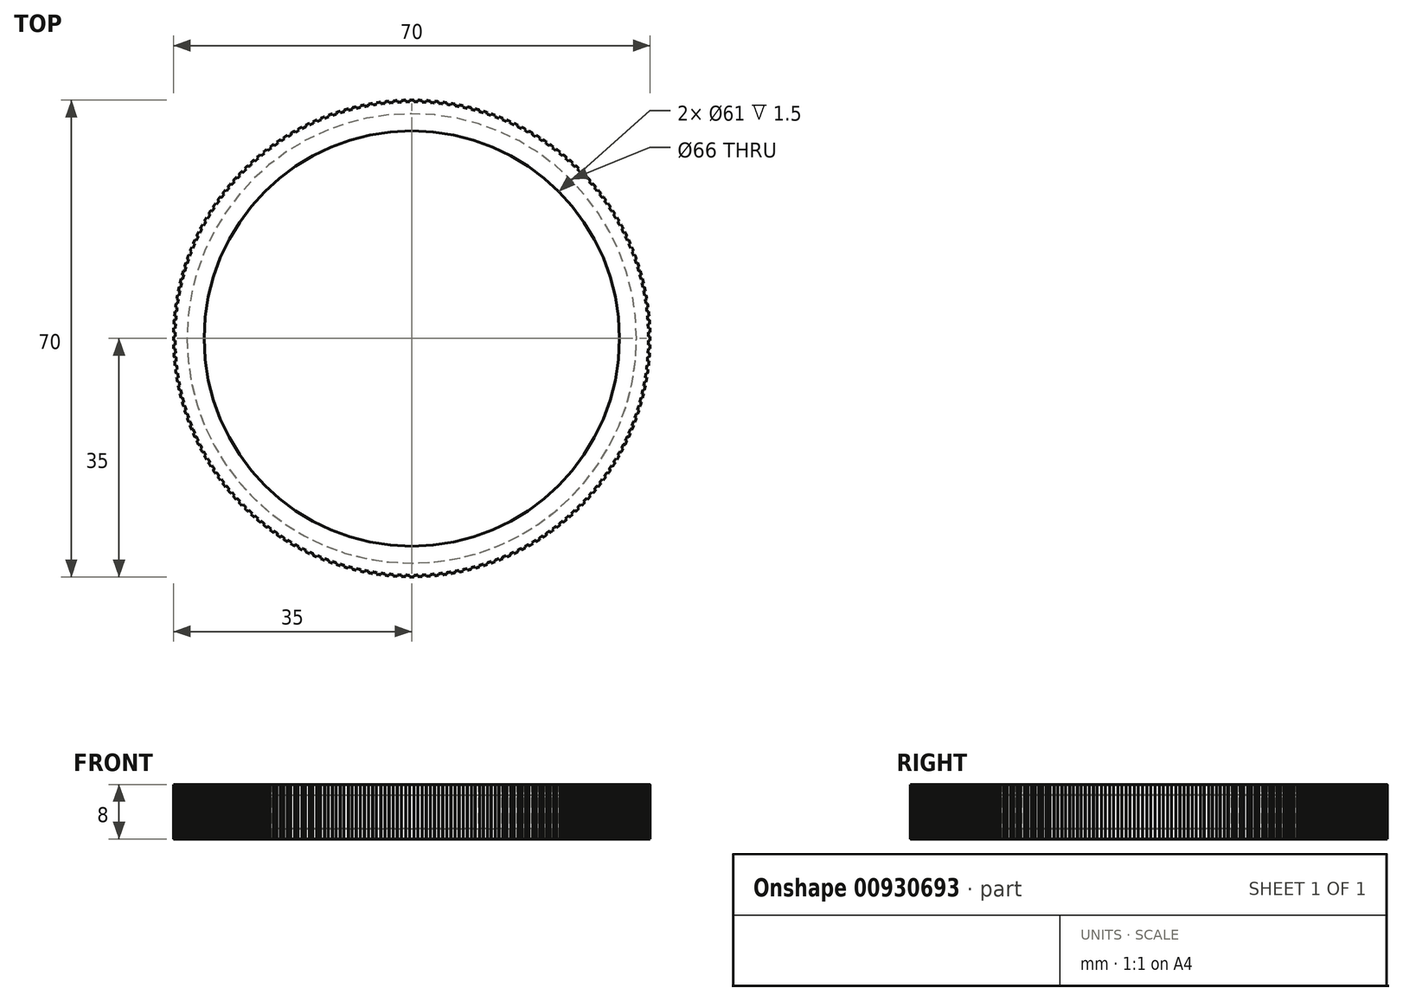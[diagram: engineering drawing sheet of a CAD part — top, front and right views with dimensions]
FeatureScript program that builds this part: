
annotation { "Feature Type Name" : "Feature", "Feature Type Description" : "" }
export const myFeature = defineFeature(function(context is Context, id is Id, definition is map)
    precondition{}
    {
        {
            var Q0;
            Q0=qCreatedBy(makeId("Front.planeOp"),FACE);
            var sketch = newSketch(context, id + "F0", { "sketchPlane" : qUnion([Q0])});
            skLineSegment(sketch, "E0.bottom", {"start": v(30.5, 8) * mm, "end": v(35, 8) * mm});
            skLineSegment(sketch, "E0.top", {"start": v(30.5, 0) * mm, "end": v(35, 0) * mm});
            skLineSegment(sketch, "E0.left", {"start": v(30.5, 8) * mm, "end": v(30.5, 6.5) * mm});
            skLineSegment(sketch, "E0.right", {"start": v(35, 8) * mm, "end": v(35, 0) * mm});
            skLineSegment(sketch, "E1", {"start": v(30.5, 6.5) * mm, "end": v(33, 6.5) * mm});
            skLineSegment(sketch, "E2", {"start": v(33, 6.5) * mm, "end": v(33, 1.5) * mm});
            skLineSegment(sketch, "E3", {"start": v(33, 1.5) * mm, "end": v(30.5, 1.5) * mm});
            skLineSegment(sketch, "E4.trimOffspring", {"start": v(30.5, 1.5) * mm, "end": v(30.5, 0) * mm});
            skLineSegment(sketch, "E5", {"start": v(0, 0) * mm, "end": v(0, 10) * mm, "construction": true});
            skSolve(sketch);
        }
        {
            var Q0;
            Q0=qSketchRegion(id+"F0",true);
            var Q1;
            Q1=sQuery(id+"F0.wireOp",EDGE,"E5");
            revolve(context, id + "F1", {"entities" : qUnion([Q0]), "axis" : qUnion([Q1]), "revolveType" : RevolveType.FULL});
        }
        {
            var Q0;
            Q0=makeQuery(id+"F1.opRevolve","SWEPT_EDGE",EDGE,{"disambiguationData":[OSD([sQuery(id+"F0.wireOp",EDGE,"E1"),sQuery(id+"F0.wireOp",EDGE,"E2")])]});
            var Q1;
            Q1=makeQuery(id+"F1.opRevolve","SWEPT_EDGE",EDGE,{"disambiguationData":[OSD([sQuery(id+"F0.wireOp",EDGE,"E2"),sQuery(id+"F0.wireOp",EDGE,"E3")])]});
            fillet(context, id + "F2", {"entities" : qUnion([Q0, Q1]), "radius" : 1 * mm, "tangentPropagation" : true, "allowEdgeOverflow" : false});
        }
        {
            var Q0;
            Q0=makeQuery(id+"F1.opRevolve","SWEPT_FACE",FACE,{"disambiguationData":[OSD([sQuery(id+"F0.wireOp",EDGE,"E0.bottom")])]});
            var sketch = newSketch(context, id + "F3", { "sketchPlane" : qUnion([Q0])});
            skLineSegment(sketch, "E6", {"start": v(0.3, 35) * mm, "end": v(0, 0) * mm, "construction": true});
            skLineSegment(sketch, "E7", {"start": v(0, 0) * mm, "end": v(0.92, 34.99) * mm, "construction": true});
            skCircle(sketch, "E8", {"center": v(0, 0) * mm, "radius": 34.75 * mm, "construction": true});
            skArc(sketch, "E9", {"start": v(0.92, 34.99) * mm, "mid": v(0.61, 35) * mm, "end": v(0.3, 35) * mm});
            skArc(sketch, "E10", {"start": v(0.9, 34.74) * mm, "mid": v(0.6, 34.74) * mm, "end": v(0.3, 34.75) * mm});
            skLineSegment(sketch, "E11", {"start": v(0.3, 35) * mm, "end": v(0.3, 34.75) * mm});
            skLineSegment(sketch, "E12", {"start": v(0.92, 34.99) * mm, "end": v(0.9, 34.74) * mm});
            skLineSegment(sketch, "E13.1.0", {"start": v(2.14, 34.93) * mm, "end": v(2.12, 34.69) * mm});
            skArc(sketch, "E13.1.1", {"start": v(2.12, 34.69) * mm, "mid": v(1.82, 34.7) * mm, "end": v(1.52, 34.72) * mm});
            skLineSegment(sketch, "E13.1.2", {"start": v(1.53, 34.97) * mm, "end": v(1.52, 34.72) * mm});
            skArc(sketch, "E13.1.3", {"start": v(2.14, 34.93) * mm, "mid": v(1.83, 34.95) * mm, "end": v(1.53, 34.97) * mm});
            skLineSegment(sketch, "E13.2.0", {"start": v(3.35, 34.84) * mm, "end": v(3.33, 34.6) * mm});
            skArc(sketch, "E13.2.1", {"start": v(3.33, 34.6) * mm, "mid": v(3.03, 34.62) * mm, "end": v(2.73, 34.64) * mm});
            skLineSegment(sketch, "E13.2.2", {"start": v(2.75, 34.9) * mm, "end": v(2.73, 34.64) * mm});
            skArc(sketch, "E13.2.3", {"start": v(3.35, 34.84) * mm, "mid": v(3.05, 34.87) * mm, "end": v(2.75, 34.9) * mm});
            skLineSegment(sketch, "E13.3.0", {"start": v(4.57, 34.7) * mm, "end": v(4.54, 34.45) * mm});
            skArc(sketch, "E13.3.1", {"start": v(4.54, 34.45) * mm, "mid": v(4.23, 34.5) * mm, "end": v(3.93, 34.53) * mm});
            skLineSegment(sketch, "E13.3.2", {"start": v(3.96, 34.78) * mm, "end": v(3.93, 34.53) * mm});
            skArc(sketch, "E13.3.3", {"start": v(4.57, 34.7) * mm, "mid": v(4.27, 34.74) * mm, "end": v(3.96, 34.78) * mm});
            skLineSegment(sketch, "E13.4.0", {"start": v(5.78, 34.52) * mm, "end": v(5.74, 34.27) * mm});
            skArc(sketch, "E13.4.1", {"start": v(5.74, 34.27) * mm, "mid": v(5.44, 34.32) * mm, "end": v(5.14, 34.37) * mm});
            skLineSegment(sketch, "E13.4.2", {"start": v(5.17, 34.62) * mm, "end": v(5.14, 34.37) * mm});
            skArc(sketch, "E13.4.3", {"start": v(5.78, 34.52) * mm, "mid": v(5.48, 34.57) * mm, "end": v(5.17, 34.62) * mm});
            skLineSegment(sketch, "E13.5.0", {"start": v(6.98, 34.3) * mm, "end": v(6.93, 34.05) * mm});
            skArc(sketch, "E13.5.1", {"start": v(6.93, 34.05) * mm, "mid": v(6.63, 34.11) * mm, "end": v(6.33, 34.17) * mm});
            skLineSegment(sketch, "E13.5.2", {"start": v(6.38, 34.41) * mm, "end": v(6.33, 34.17) * mm});
            skArc(sketch, "E13.5.3", {"start": v(6.98, 34.3) * mm, "mid": v(6.68, 34.36) * mm, "end": v(6.38, 34.41) * mm});
            skLineSegment(sketch, "E13.6.0", {"start": v(8.17, 34.03) * mm, "end": v(8.11, 33.79) * mm});
            skArc(sketch, "E13.6.1", {"start": v(8.11, 33.79) * mm, "mid": v(7.82, 33.86) * mm, "end": v(7.52, 33.93) * mm});
            skLineSegment(sketch, "E13.6.2", {"start": v(7.58, 34.17) * mm, "end": v(7.52, 33.93) * mm});
            skArc(sketch, "E13.6.3", {"start": v(8.17, 34.03) * mm, "mid": v(7.87, 34.1) * mm, "end": v(7.58, 34.17) * mm});
            skLineSegment(sketch, "E13.7.0", {"start": v(9.35, 33.73) * mm, "end": v(9.29, 33.49) * mm});
            skArc(sketch, "E13.7.1", {"start": v(9.29, 33.49) * mm, "mid": v(9, 33.57) * mm, "end": v(8.7, 33.64) * mm});
            skLineSegment(sketch, "E13.7.2", {"start": v(8.76, 33.89) * mm, "end": v(8.7, 33.64) * mm});
            skArc(sketch, "E13.7.3", {"start": v(9.35, 33.73) * mm, "mid": v(9.06, 33.8) * mm, "end": v(8.76, 33.89) * mm});
            skLineSegment(sketch, "E13.8.0", {"start": v(10.52, 33.38) * mm, "end": v(10.45, 33.14) * mm});
            skArc(sketch, "E13.8.1", {"start": v(10.45, 33.14) * mm, "mid": v(10.16, 33.23) * mm, "end": v(9.87, 33.32) * mm});
            skLineSegment(sketch, "E13.8.2", {"start": v(9.94, 33.56) * mm, "end": v(9.87, 33.32) * mm});
            skArc(sketch, "E13.8.3", {"start": v(10.52, 33.38) * mm, "mid": v(10.23, 33.47) * mm, "end": v(9.94, 33.56) * mm});
            skLineSegment(sketch, "E13.9.0", {"start": v(11.68, 33) * mm, "end": v(11.6, 32.76) * mm});
            skArc(sketch, "E13.9.1", {"start": v(11.6, 32.76) * mm, "mid": v(11.31, 32.86) * mm, "end": v(11.03, 32.95) * mm});
            skLineSegment(sketch, "E13.9.2", {"start": v(11.1, 33.2) * mm, "end": v(11.03, 32.95) * mm});
            skArc(sketch, "E13.9.3", {"start": v(11.68, 33) * mm, "mid": v(11.4, 33.1) * mm, "end": v(11.1, 33.2) * mm});
            skLineSegment(sketch, "E13.10.0", {"start": v(12.83, 32.56) * mm, "end": v(12.74, 32.33) * mm});
            skArc(sketch, "E13.10.1", {"start": v(12.74, 32.33) * mm, "mid": v(12.45, 32.44) * mm, "end": v(12.17, 32.55) * mm});
            skLineSegment(sketch, "E13.10.2", {"start": v(12.26, 32.78) * mm, "end": v(12.17, 32.55) * mm});
            skArc(sketch, "E13.10.3", {"start": v(12.83, 32.56) * mm, "mid": v(12.54, 32.68) * mm, "end": v(12.26, 32.78) * mm});
            skLineSegment(sketch, "E13.11.0", {"start": v(13.96, 32.1) * mm, "end": v(13.86, 31.87) * mm});
            skArc(sketch, "E13.11.1", {"start": v(13.86, 31.87) * mm, "mid": v(13.58, 31.99) * mm, "end": v(13.3, 32.1) * mm});
            skLineSegment(sketch, "E13.11.2", {"start": v(13.4, 32.34) * mm, "end": v(13.3, 32.1) * mm});
            skArc(sketch, "E13.11.3", {"start": v(13.96, 32.1) * mm, "mid": v(13.68, 32.22) * mm, "end": v(13.4, 32.34) * mm});
            skLineSegment(sketch, "E13.12.0", {"start": v(15.07, 31.6) * mm, "end": v(14.96, 31.36) * mm});
            skArc(sketch, "E13.12.1", {"start": v(14.96, 31.36) * mm, "mid": v(14.69, 31.5) * mm, "end": v(14.41, 31.62) * mm});
            skLineSegment(sketch, "E13.12.2", {"start": v(14.51, 31.85) * mm, "end": v(14.41, 31.62) * mm});
            skArc(sketch, "E13.12.3", {"start": v(15.07, 31.6) * mm, "mid": v(14.8, 31.72) * mm, "end": v(14.51, 31.85) * mm});
            skLineSegment(sketch, "E13.13.0", {"start": v(16.16, 31.05) * mm, "end": v(16.05, 30.82) * mm});
            skArc(sketch, "E13.13.1", {"start": v(16.05, 30.82) * mm, "mid": v(15.78, 30.96) * mm, "end": v(15.5, 31.1) * mm});
            skLineSegment(sketch, "E13.13.2", {"start": v(15.62, 31.32) * mm, "end": v(15.5, 31.1) * mm});
            skArc(sketch, "E13.13.3", {"start": v(16.16, 31.05) * mm, "mid": v(15.89, 31.19) * mm, "end": v(15.62, 31.32) * mm});
            skLineSegment(sketch, "E13.14.0", {"start": v(17.23, 30.46) * mm, "end": v(17.11, 30.24) * mm});
            skArc(sketch, "E13.14.1", {"start": v(17.11, 30.24) * mm, "mid": v(16.85, 30.4) * mm, "end": v(16.58, 30.54) * mm});
            skLineSegment(sketch, "E13.14.2", {"start": v(16.7, 30.76) * mm, "end": v(16.58, 30.54) * mm});
            skArc(sketch, "E13.14.3", {"start": v(17.23, 30.46) * mm, "mid": v(16.97, 30.61) * mm, "end": v(16.7, 30.76) * mm});
            skLineSegment(sketch, "E13.15.0", {"start": v(18.29, 29.84) * mm, "end": v(18.16, 29.63) * mm});
            skArc(sketch, "E13.15.1", {"start": v(18.16, 29.63) * mm, "mid": v(17.9, 29.79) * mm, "end": v(17.64, 29.94) * mm});
            skLineSegment(sketch, "E13.15.2", {"start": v(17.76, 30.16) * mm, "end": v(17.64, 29.94) * mm});
            skArc(sketch, "E13.15.3", {"start": v(18.29, 29.84) * mm, "mid": v(18.03, 30) * mm, "end": v(17.76, 30.16) * mm});
            skLineSegment(sketch, "E13.16.0", {"start": v(19.32, 29.19) * mm, "end": v(19.18, 28.98) * mm});
            skArc(sketch, "E13.16.1", {"start": v(19.18, 28.98) * mm, "mid": v(18.93, 29.14) * mm, "end": v(18.67, 29.3) * mm});
            skLineSegment(sketch, "E13.16.2", {"start": v(18.8, 29.52) * mm, "end": v(18.67, 29.3) * mm});
            skArc(sketch, "E13.16.3", {"start": v(19.32, 29.19) * mm, "mid": v(19.06, 29.35) * mm, "end": v(18.8, 29.52) * mm});
            skLineSegment(sketch, "E13.17.0", {"start": v(20.32, 28.5) * mm, "end": v(20.18, 28.3) * mm});
            skArc(sketch, "E13.17.1", {"start": v(20.18, 28.3) * mm, "mid": v(19.93, 28.47) * mm, "end": v(19.68, 28.64) * mm});
            skLineSegment(sketch, "E13.17.2", {"start": v(19.82, 28.84) * mm, "end": v(19.68, 28.64) * mm});
            skArc(sketch, "E13.17.3", {"start": v(20.32, 28.5) * mm, "mid": v(20.08, 28.67) * mm, "end": v(19.82, 28.84) * mm});
            skLineSegment(sketch, "E13.18.0", {"start": v(21.3, 27.77) * mm, "end": v(21.15, 27.57) * mm});
            skArc(sketch, "E13.18.1", {"start": v(21.15, 27.57) * mm, "mid": v(20.91, 27.75) * mm, "end": v(20.67, 27.93) * mm});
            skLineSegment(sketch, "E13.18.2", {"start": v(20.82, 28.13) * mm, "end": v(20.67, 27.93) * mm});
            skArc(sketch, "E13.18.3", {"start": v(21.3, 27.77) * mm, "mid": v(21.06, 27.95) * mm, "end": v(20.82, 28.13) * mm});
            skLineSegment(sketch, "E13.19.0", {"start": v(22.26, 27) * mm, "end": v(22.1, 26.81) * mm});
            skArc(sketch, "E13.19.1", {"start": v(22.1, 26.81) * mm, "mid": v(21.87, 27) * mm, "end": v(21.63, 27.2) * mm});
            skLineSegment(sketch, "E13.19.2", {"start": v(21.79, 27.4) * mm, "end": v(21.63, 27.2) * mm});
            skArc(sketch, "E13.19.3", {"start": v(22.26, 27) * mm, "mid": v(22.03, 27.2) * mm, "end": v(21.79, 27.4) * mm});
            skLineSegment(sketch, "E13.20.0", {"start": v(23.2, 26.21) * mm, "end": v(23.03, 26.03) * mm});
            skArc(sketch, "E13.20.1", {"start": v(23.03, 26.03) * mm, "mid": v(22.8, 26.23) * mm, "end": v(22.57, 26.42) * mm});
            skLineSegment(sketch, "E13.20.2", {"start": v(22.73, 26.61) * mm, "end": v(22.57, 26.42) * mm});
            skArc(sketch, "E13.20.3", {"start": v(23.2, 26.21) * mm, "mid": v(22.96, 26.41) * mm, "end": v(22.73, 26.61) * mm});
            skLineSegment(sketch, "E13.21.0", {"start": v(24.1, 25.39) * mm, "end": v(23.92, 25.2) * mm});
            skArc(sketch, "E13.21.1", {"start": v(23.92, 25.2) * mm, "mid": v(23.7, 25.41) * mm, "end": v(23.48, 25.62) * mm});
            skLineSegment(sketch, "E13.21.2", {"start": v(23.65, 25.8) * mm, "end": v(23.48, 25.62) * mm});
            skArc(sketch, "E13.21.3", {"start": v(24.1, 25.39) * mm, "mid": v(23.87, 25.6) * mm, "end": v(23.65, 25.8) * mm});
            skLineSegment(sketch, "E13.22.0", {"start": v(24.96, 24.53) * mm, "end": v(24.79, 24.36) * mm});
            skArc(sketch, "E13.22.1", {"start": v(24.79, 24.36) * mm, "mid": v(24.57, 24.57) * mm, "end": v(24.36, 24.79) * mm});
            skLineSegment(sketch, "E13.22.2", {"start": v(24.53, 24.96) * mm, "end": v(24.36, 24.79) * mm});
            skArc(sketch, "E13.22.3", {"start": v(24.96, 24.53) * mm, "mid": v(24.75, 24.75) * mm, "end": v(24.53, 24.96) * mm});
            skLineSegment(sketch, "E13.23.0", {"start": v(25.8, 23.65) * mm, "end": v(25.62, 23.48) * mm});
            skArc(sketch, "E13.23.1", {"start": v(25.62, 23.48) * mm, "mid": v(25.41, 23.7) * mm, "end": v(25.2, 23.92) * mm});
            skLineSegment(sketch, "E13.23.2", {"start": v(25.39, 24.1) * mm, "end": v(25.2, 23.92) * mm});
            skArc(sketch, "E13.23.3", {"start": v(25.8, 23.65) * mm, "mid": v(25.6, 23.87) * mm, "end": v(25.39, 24.1) * mm});
            skLineSegment(sketch, "E13.24.0", {"start": v(26.61, 22.73) * mm, "end": v(26.42, 22.57) * mm});
            skArc(sketch, "E13.24.1", {"start": v(26.42, 22.57) * mm, "mid": v(26.23, 22.8) * mm, "end": v(26.03, 23.03) * mm});
            skLineSegment(sketch, "E13.24.2", {"start": v(26.21, 23.2) * mm, "end": v(26.03, 23.03) * mm});
            skArc(sketch, "E13.24.3", {"start": v(26.61, 22.73) * mm, "mid": v(26.41, 22.96) * mm, "end": v(26.21, 23.2) * mm});
            skLineSegment(sketch, "E13.25.0", {"start": v(27.4, 21.79) * mm, "end": v(27.2, 21.63) * mm});
            skArc(sketch, "E13.25.1", {"start": v(27.2, 21.63) * mm, "mid": v(27, 21.87) * mm, "end": v(26.81, 22.1) * mm});
            skLineSegment(sketch, "E13.25.2", {"start": v(27, 22.26) * mm, "end": v(26.81, 22.1) * mm});
            skArc(sketch, "E13.25.3", {"start": v(27.4, 21.79) * mm, "mid": v(27.2, 22.03) * mm, "end": v(27, 22.26) * mm});
            skLineSegment(sketch, "E13.26.0", {"start": v(28.13, 20.82) * mm, "end": v(27.93, 20.67) * mm});
            skArc(sketch, "E13.26.1", {"start": v(27.93, 20.67) * mm, "mid": v(27.75, 20.91) * mm, "end": v(27.57, 21.15) * mm});
            skLineSegment(sketch, "E13.26.2", {"start": v(27.77, 21.3) * mm, "end": v(27.57, 21.15) * mm});
            skArc(sketch, "E13.26.3", {"start": v(28.13, 20.82) * mm, "mid": v(27.95, 21.06) * mm, "end": v(27.77, 21.3) * mm});
            skLineSegment(sketch, "E13.27.0", {"start": v(28.84, 19.82) * mm, "end": v(28.64, 19.68) * mm});
            skArc(sketch, "E13.27.1", {"start": v(28.64, 19.68) * mm, "mid": v(28.47, 19.93) * mm, "end": v(28.3, 20.18) * mm});
            skLineSegment(sketch, "E13.27.2", {"start": v(28.5, 20.32) * mm, "end": v(28.3, 20.18) * mm});
            skArc(sketch, "E13.27.3", {"start": v(28.84, 19.82) * mm, "mid": v(28.67, 20.08) * mm, "end": v(28.5, 20.32) * mm});
            skLineSegment(sketch, "E13.28.0", {"start": v(29.52, 18.8) * mm, "end": v(29.3, 18.67) * mm});
            skArc(sketch, "E13.28.1", {"start": v(29.3, 18.67) * mm, "mid": v(29.14, 18.93) * mm, "end": v(28.98, 19.18) * mm});
            skLineSegment(sketch, "E13.28.2", {"start": v(29.19, 19.32) * mm, "end": v(28.98, 19.18) * mm});
            skArc(sketch, "E13.28.3", {"start": v(29.52, 18.8) * mm, "mid": v(29.35, 19.06) * mm, "end": v(29.19, 19.32) * mm});
            skLineSegment(sketch, "E13.29.0", {"start": v(30.16, 17.76) * mm, "end": v(29.94, 17.64) * mm});
            skArc(sketch, "E13.29.1", {"start": v(29.94, 17.64) * mm, "mid": v(29.79, 17.9) * mm, "end": v(29.63, 18.16) * mm});
            skLineSegment(sketch, "E13.29.2", {"start": v(29.84, 18.29) * mm, "end": v(29.63, 18.16) * mm});
            skArc(sketch, "E13.29.3", {"start": v(30.16, 17.76) * mm, "mid": v(30, 18.03) * mm, "end": v(29.84, 18.29) * mm});
            skLineSegment(sketch, "E13.30.0", {"start": v(30.76, 16.7) * mm, "end": v(30.54, 16.58) * mm});
            skArc(sketch, "E13.30.1", {"start": v(30.54, 16.58) * mm, "mid": v(30.4, 16.85) * mm, "end": v(30.24, 17.11) * mm});
            skLineSegment(sketch, "E13.30.2", {"start": v(30.46, 17.23) * mm, "end": v(30.24, 17.11) * mm});
            skArc(sketch, "E13.30.3", {"start": v(30.76, 16.7) * mm, "mid": v(30.61, 16.97) * mm, "end": v(30.46, 17.23) * mm});
            skLineSegment(sketch, "E13.31.0", {"start": v(31.32, 15.62) * mm, "end": v(31.1, 15.5) * mm});
            skArc(sketch, "E13.31.1", {"start": v(31.1, 15.5) * mm, "mid": v(30.96, 15.78) * mm, "end": v(30.82, 16.05) * mm});
            skLineSegment(sketch, "E13.31.2", {"start": v(31.05, 16.16) * mm, "end": v(30.82, 16.05) * mm});
            skArc(sketch, "E13.31.3", {"start": v(31.32, 15.62) * mm, "mid": v(31.19, 15.89) * mm, "end": v(31.05, 16.16) * mm});
            skLineSegment(sketch, "E13.32.0", {"start": v(31.85, 14.51) * mm, "end": v(31.62, 14.41) * mm});
            skArc(sketch, "E13.32.1", {"start": v(31.62, 14.41) * mm, "mid": v(31.5, 14.69) * mm, "end": v(31.36, 14.96) * mm});
            skLineSegment(sketch, "E13.32.2", {"start": v(31.6, 15.07) * mm, "end": v(31.36, 14.96) * mm});
            skArc(sketch, "E13.32.3", {"start": v(31.85, 14.51) * mm, "mid": v(31.72, 14.8) * mm, "end": v(31.6, 15.07) * mm});
            skLineSegment(sketch, "E13.33.0", {"start": v(32.34, 13.4) * mm, "end": v(32.1, 13.3) * mm});
            skArc(sketch, "E13.33.1", {"start": v(32.1, 13.3) * mm, "mid": v(31.99, 13.58) * mm, "end": v(31.87, 13.86) * mm});
            skLineSegment(sketch, "E13.33.2", {"start": v(32.1, 13.96) * mm, "end": v(31.87, 13.86) * mm});
            skArc(sketch, "E13.33.3", {"start": v(32.34, 13.4) * mm, "mid": v(32.22, 13.68) * mm, "end": v(32.1, 13.96) * mm});
            skLineSegment(sketch, "E13.34.0", {"start": v(32.78, 12.26) * mm, "end": v(32.55, 12.17) * mm});
            skArc(sketch, "E13.34.1", {"start": v(32.55, 12.17) * mm, "mid": v(32.44, 12.45) * mm, "end": v(32.33, 12.74) * mm});
            skLineSegment(sketch, "E13.34.2", {"start": v(32.56, 12.83) * mm, "end": v(32.33, 12.74) * mm});
            skArc(sketch, "E13.34.3", {"start": v(32.78, 12.26) * mm, "mid": v(32.68, 12.54) * mm, "end": v(32.56, 12.83) * mm});
            skLineSegment(sketch, "E13.35.0", {"start": v(33.2, 11.1) * mm, "end": v(32.95, 11.03) * mm});
            skArc(sketch, "E13.35.1", {"start": v(32.95, 11.03) * mm, "mid": v(32.86, 11.31) * mm, "end": v(32.76, 11.6) * mm});
            skLineSegment(sketch, "E13.35.2", {"start": v(33, 11.68) * mm, "end": v(32.76, 11.6) * mm});
            skArc(sketch, "E13.35.3", {"start": v(33.2, 11.1) * mm, "mid": v(33.1, 11.4) * mm, "end": v(33, 11.68) * mm});
            skLineSegment(sketch, "E13.36.0", {"start": v(33.56, 9.94) * mm, "end": v(33.32, 9.87) * mm});
            skArc(sketch, "E13.36.1", {"start": v(33.32, 9.87) * mm, "mid": v(33.23, 10.16) * mm, "end": v(33.14, 10.45) * mm});
            skLineSegment(sketch, "E13.36.2", {"start": v(33.38, 10.52) * mm, "end": v(33.14, 10.45) * mm});
            skArc(sketch, "E13.36.3", {"start": v(33.56, 9.94) * mm, "mid": v(33.47, 10.23) * mm, "end": v(33.38, 10.52) * mm});
            skLineSegment(sketch, "E13.37.0", {"start": v(33.89, 8.76) * mm, "end": v(33.64, 8.7) * mm});
            skArc(sketch, "E13.37.1", {"start": v(33.64, 8.7) * mm, "mid": v(33.57, 9) * mm, "end": v(33.49, 9.29) * mm});
            skLineSegment(sketch, "E13.37.2", {"start": v(33.73, 9.35) * mm, "end": v(33.49, 9.29) * mm});
            skArc(sketch, "E13.37.3", {"start": v(33.89, 8.76) * mm, "mid": v(33.8, 9.06) * mm, "end": v(33.73, 9.35) * mm});
            skLineSegment(sketch, "E13.38.0", {"start": v(34.17, 7.58) * mm, "end": v(33.93, 7.52) * mm});
            skArc(sketch, "E13.38.1", {"start": v(33.93, 7.52) * mm, "mid": v(33.86, 7.82) * mm, "end": v(33.79, 8.11) * mm});
            skLineSegment(sketch, "E13.38.2", {"start": v(34.03, 8.17) * mm, "end": v(33.79, 8.11) * mm});
            skArc(sketch, "E13.38.3", {"start": v(34.17, 7.58) * mm, "mid": v(34.1, 7.87) * mm, "end": v(34.03, 8.17) * mm});
            skLineSegment(sketch, "E13.39.0", {"start": v(34.41, 6.38) * mm, "end": v(34.17, 6.33) * mm});
            skArc(sketch, "E13.39.1", {"start": v(34.17, 6.33) * mm, "mid": v(34.11, 6.63) * mm, "end": v(34.05, 6.93) * mm});
            skLineSegment(sketch, "E13.39.2", {"start": v(34.3, 6.98) * mm, "end": v(34.05, 6.93) * mm});
            skArc(sketch, "E13.39.3", {"start": v(34.41, 6.38) * mm, "mid": v(34.36, 6.68) * mm, "end": v(34.3, 6.98) * mm});
            skLineSegment(sketch, "E13.40.0", {"start": v(34.62, 5.17) * mm, "end": v(34.37, 5.14) * mm});
            skArc(sketch, "E13.40.1", {"start": v(34.37, 5.14) * mm, "mid": v(34.32, 5.44) * mm, "end": v(34.27, 5.74) * mm});
            skLineSegment(sketch, "E13.40.2", {"start": v(34.52, 5.78) * mm, "end": v(34.27, 5.74) * mm});
            skArc(sketch, "E13.40.3", {"start": v(34.62, 5.17) * mm, "mid": v(34.57, 5.48) * mm, "end": v(34.52, 5.78) * mm});
            skLineSegment(sketch, "E13.41.0", {"start": v(34.78, 3.96) * mm, "end": v(34.53, 3.93) * mm});
            skArc(sketch, "E13.41.1", {"start": v(34.53, 3.93) * mm, "mid": v(34.5, 4.23) * mm, "end": v(34.45, 4.54) * mm});
            skLineSegment(sketch, "E13.41.2", {"start": v(34.7, 4.57) * mm, "end": v(34.45, 4.54) * mm});
            skArc(sketch, "E13.41.3", {"start": v(34.78, 3.96) * mm, "mid": v(34.74, 4.27) * mm, "end": v(34.7, 4.57) * mm});
            skLineSegment(sketch, "E13.42.0", {"start": v(34.9, 2.75) * mm, "end": v(34.64, 2.73) * mm});
            skArc(sketch, "E13.42.1", {"start": v(34.64, 2.73) * mm, "mid": v(34.62, 3.03) * mm, "end": v(34.6, 3.33) * mm});
            skLineSegment(sketch, "E13.42.2", {"start": v(34.84, 3.35) * mm, "end": v(34.6, 3.33) * mm});
            skArc(sketch, "E13.42.3", {"start": v(34.9, 2.75) * mm, "mid": v(34.87, 3.05) * mm, "end": v(34.84, 3.35) * mm});
            skLineSegment(sketch, "E13.43.0", {"start": v(34.97, 1.53) * mm, "end": v(34.72, 1.52) * mm});
            skArc(sketch, "E13.43.1", {"start": v(34.72, 1.52) * mm, "mid": v(34.7, 1.82) * mm, "end": v(34.69, 2.12) * mm});
            skLineSegment(sketch, "E13.43.2", {"start": v(34.93, 2.14) * mm, "end": v(34.69, 2.12) * mm});
            skArc(sketch, "E13.43.3", {"start": v(34.97, 1.53) * mm, "mid": v(34.95, 1.83) * mm, "end": v(34.93, 2.14) * mm});
            skLineSegment(sketch, "E13.44.0", {"start": v(35, 0.3) * mm, "end": v(34.75, 0.3) * mm});
            skArc(sketch, "E13.44.1", {"start": v(34.75, 0.3) * mm, "mid": v(34.74, 0.6) * mm, "end": v(34.74, 0.9) * mm});
            skLineSegment(sketch, "E13.44.2", {"start": v(34.99, 0.92) * mm, "end": v(34.74, 0.9) * mm});
            skArc(sketch, "E13.44.3", {"start": v(35, 0.3) * mm, "mid": v(35, 0.61) * mm, "end": v(34.99, 0.92) * mm});
            skLineSegment(sketch, "E13.45.0", {"start": v(34.99, -0.92) * mm, "end": v(34.74, -0.9) * mm});
            skArc(sketch, "E13.45.1", {"start": v(34.74, -0.9) * mm, "mid": v(34.74, -0.6) * mm, "end": v(34.75, -0.3) * mm});
            skLineSegment(sketch, "E13.45.2", {"start": v(35, -0.3) * mm, "end": v(34.75, -0.3) * mm});
            skArc(sketch, "E13.45.3", {"start": v(34.99, -0.92) * mm, "mid": v(35, -0.61) * mm, "end": v(35, -0.3) * mm});
            skLineSegment(sketch, "E13.46.0", {"start": v(34.93, -2.14) * mm, "end": v(34.69, -2.12) * mm});
            skArc(sketch, "E13.46.1", {"start": v(34.69, -2.12) * mm, "mid": v(34.7, -1.82) * mm, "end": v(34.72, -1.52) * mm});
            skLineSegment(sketch, "E13.46.2", {"start": v(34.97, -1.53) * mm, "end": v(34.72, -1.52) * mm});
            skArc(sketch, "E13.46.3", {"start": v(34.93, -2.14) * mm, "mid": v(34.95, -1.83) * mm, "end": v(34.97, -1.53) * mm});
            skLineSegment(sketch, "E13.47.0", {"start": v(34.84, -3.35) * mm, "end": v(34.6, -3.33) * mm});
            skArc(sketch, "E13.47.1", {"start": v(34.6, -3.33) * mm, "mid": v(34.62, -3.03) * mm, "end": v(34.64, -2.73) * mm});
            skLineSegment(sketch, "E13.47.2", {"start": v(34.9, -2.75) * mm, "end": v(34.64, -2.73) * mm});
            skArc(sketch, "E13.47.3", {"start": v(34.84, -3.35) * mm, "mid": v(34.87, -3.05) * mm, "end": v(34.9, -2.75) * mm});
            skLineSegment(sketch, "E13.48.0", {"start": v(34.7, -4.57) * mm, "end": v(34.45, -4.54) * mm});
            skArc(sketch, "E13.48.1", {"start": v(34.45, -4.54) * mm, "mid": v(34.5, -4.23) * mm, "end": v(34.53, -3.93) * mm});
            skLineSegment(sketch, "E13.48.2", {"start": v(34.78, -3.96) * mm, "end": v(34.53, -3.93) * mm});
            skArc(sketch, "E13.48.3", {"start": v(34.7, -4.57) * mm, "mid": v(34.74, -4.27) * mm, "end": v(34.78, -3.96) * mm});
            skLineSegment(sketch, "E13.49.0", {"start": v(34.52, -5.78) * mm, "end": v(34.27, -5.74) * mm});
            skArc(sketch, "E13.49.1", {"start": v(34.27, -5.74) * mm, "mid": v(34.32, -5.44) * mm, "end": v(34.37, -5.14) * mm});
            skLineSegment(sketch, "E13.49.2", {"start": v(34.62, -5.17) * mm, "end": v(34.37, -5.14) * mm});
            skArc(sketch, "E13.49.3", {"start": v(34.52, -5.78) * mm, "mid": v(34.57, -5.48) * mm, "end": v(34.62, -5.17) * mm});
            skLineSegment(sketch, "E13.50.0", {"start": v(34.3, -6.98) * mm, "end": v(34.05, -6.93) * mm});
            skArc(sketch, "E13.50.1", {"start": v(34.05, -6.93) * mm, "mid": v(34.11, -6.63) * mm, "end": v(34.17, -6.33) * mm});
            skLineSegment(sketch, "E13.50.2", {"start": v(34.41, -6.38) * mm, "end": v(34.17, -6.33) * mm});
            skArc(sketch, "E13.50.3", {"start": v(34.3, -6.98) * mm, "mid": v(34.36, -6.68) * mm, "end": v(34.41, -6.38) * mm});
            skLineSegment(sketch, "E13.51.0", {"start": v(34.03, -8.17) * mm, "end": v(33.79, -8.11) * mm});
            skArc(sketch, "E13.51.1", {"start": v(33.79, -8.11) * mm, "mid": v(33.86, -7.82) * mm, "end": v(33.93, -7.52) * mm});
            skLineSegment(sketch, "E13.51.2", {"start": v(34.17, -7.58) * mm, "end": v(33.93, -7.52) * mm});
            skArc(sketch, "E13.51.3", {"start": v(34.03, -8.17) * mm, "mid": v(34.1, -7.87) * mm, "end": v(34.17, -7.58) * mm});
            skLineSegment(sketch, "E13.52.0", {"start": v(33.73, -9.35) * mm, "end": v(33.49, -9.29) * mm});
            skArc(sketch, "E13.52.1", {"start": v(33.49, -9.29) * mm, "mid": v(33.57, -9) * mm, "end": v(33.64, -8.7) * mm});
            skLineSegment(sketch, "E13.52.2", {"start": v(33.89, -8.76) * mm, "end": v(33.64, -8.7) * mm});
            skArc(sketch, "E13.52.3", {"start": v(33.73, -9.35) * mm, "mid": v(33.8, -9.06) * mm, "end": v(33.89, -8.76) * mm});
            skLineSegment(sketch, "E13.53.0", {"start": v(33.38, -10.52) * mm, "end": v(33.14, -10.45) * mm});
            skArc(sketch, "E13.53.1", {"start": v(33.14, -10.45) * mm, "mid": v(33.23, -10.16) * mm, "end": v(33.32, -9.87) * mm});
            skLineSegment(sketch, "E13.53.2", {"start": v(33.56, -9.94) * mm, "end": v(33.32, -9.87) * mm});
            skArc(sketch, "E13.53.3", {"start": v(33.38, -10.52) * mm, "mid": v(33.47, -10.23) * mm, "end": v(33.56, -9.94) * mm});
            skLineSegment(sketch, "E13.54.0", {"start": v(33, -11.68) * mm, "end": v(32.76, -11.6) * mm});
            skArc(sketch, "E13.54.1", {"start": v(32.76, -11.6) * mm, "mid": v(32.86, -11.31) * mm, "end": v(32.95, -11.03) * mm});
            skLineSegment(sketch, "E13.54.2", {"start": v(33.2, -11.1) * mm, "end": v(32.95, -11.03) * mm});
            skArc(sketch, "E13.54.3", {"start": v(33, -11.68) * mm, "mid": v(33.1, -11.4) * mm, "end": v(33.2, -11.1) * mm});
            skLineSegment(sketch, "E13.55.0", {"start": v(32.56, -12.83) * mm, "end": v(32.33, -12.74) * mm});
            skArc(sketch, "E13.55.1", {"start": v(32.33, -12.74) * mm, "mid": v(32.44, -12.45) * mm, "end": v(32.55, -12.17) * mm});
            skLineSegment(sketch, "E13.55.2", {"start": v(32.78, -12.26) * mm, "end": v(32.55, -12.17) * mm});
            skArc(sketch, "E13.55.3", {"start": v(32.56, -12.83) * mm, "mid": v(32.68, -12.54) * mm, "end": v(32.78, -12.26) * mm});
            skLineSegment(sketch, "E13.56.0", {"start": v(32.1, -13.96) * mm, "end": v(31.87, -13.86) * mm});
            skArc(sketch, "E13.56.1", {"start": v(31.87, -13.86) * mm, "mid": v(31.99, -13.58) * mm, "end": v(32.1, -13.3) * mm});
            skLineSegment(sketch, "E13.56.2", {"start": v(32.34, -13.4) * mm, "end": v(32.1, -13.3) * mm});
            skArc(sketch, "E13.56.3", {"start": v(32.1, -13.96) * mm, "mid": v(32.22, -13.68) * mm, "end": v(32.34, -13.4) * mm});
            skLineSegment(sketch, "E13.57.0", {"start": v(31.6, -15.07) * mm, "end": v(31.36, -14.96) * mm});
            skArc(sketch, "E13.57.1", {"start": v(31.36, -14.96) * mm, "mid": v(31.5, -14.69) * mm, "end": v(31.62, -14.41) * mm});
            skLineSegment(sketch, "E13.57.2", {"start": v(31.85, -14.51) * mm, "end": v(31.62, -14.41) * mm});
            skArc(sketch, "E13.57.3", {"start": v(31.6, -15.07) * mm, "mid": v(31.72, -14.8) * mm, "end": v(31.85, -14.51) * mm});
            skLineSegment(sketch, "E13.58.0", {"start": v(31.05, -16.16) * mm, "end": v(30.82, -16.05) * mm});
            skArc(sketch, "E13.58.1", {"start": v(30.82, -16.05) * mm, "mid": v(30.96, -15.78) * mm, "end": v(31.1, -15.5) * mm});
            skLineSegment(sketch, "E13.58.2", {"start": v(31.32, -15.62) * mm, "end": v(31.1, -15.5) * mm});
            skArc(sketch, "E13.58.3", {"start": v(31.05, -16.16) * mm, "mid": v(31.19, -15.89) * mm, "end": v(31.32, -15.62) * mm});
            skLineSegment(sketch, "E13.59.0", {"start": v(30.46, -17.23) * mm, "end": v(30.24, -17.11) * mm});
            skArc(sketch, "E13.59.1", {"start": v(30.24, -17.11) * mm, "mid": v(30.4, -16.85) * mm, "end": v(30.54, -16.58) * mm});
            skLineSegment(sketch, "E13.59.2", {"start": v(30.76, -16.7) * mm, "end": v(30.54, -16.58) * mm});
            skArc(sketch, "E13.59.3", {"start": v(30.46, -17.23) * mm, "mid": v(30.61, -16.97) * mm, "end": v(30.76, -16.7) * mm});
            skLineSegment(sketch, "E13.60.0", {"start": v(29.84, -18.29) * mm, "end": v(29.63, -18.16) * mm});
            skArc(sketch, "E13.60.1", {"start": v(29.63, -18.16) * mm, "mid": v(29.79, -17.9) * mm, "end": v(29.94, -17.64) * mm});
            skLineSegment(sketch, "E13.60.2", {"start": v(30.16, -17.76) * mm, "end": v(29.94, -17.64) * mm});
            skArc(sketch, "E13.60.3", {"start": v(29.84, -18.29) * mm, "mid": v(30, -18.03) * mm, "end": v(30.16, -17.76) * mm});
            skLineSegment(sketch, "E13.61.0", {"start": v(29.19, -19.32) * mm, "end": v(28.98, -19.18) * mm});
            skArc(sketch, "E13.61.1", {"start": v(28.98, -19.18) * mm, "mid": v(29.14, -18.93) * mm, "end": v(29.3, -18.67) * mm});
            skLineSegment(sketch, "E13.61.2", {"start": v(29.52, -18.8) * mm, "end": v(29.3, -18.67) * mm});
            skArc(sketch, "E13.61.3", {"start": v(29.19, -19.32) * mm, "mid": v(29.35, -19.06) * mm, "end": v(29.52, -18.8) * mm});
            skLineSegment(sketch, "E13.62.0", {"start": v(28.5, -20.32) * mm, "end": v(28.3, -20.18) * mm});
            skArc(sketch, "E13.62.1", {"start": v(28.3, -20.18) * mm, "mid": v(28.47, -19.93) * mm, "end": v(28.64, -19.68) * mm});
            skLineSegment(sketch, "E13.62.2", {"start": v(28.84, -19.82) * mm, "end": v(28.64, -19.68) * mm});
            skArc(sketch, "E13.62.3", {"start": v(28.5, -20.32) * mm, "mid": v(28.67, -20.08) * mm, "end": v(28.84, -19.82) * mm});
            skLineSegment(sketch, "E13.63.0", {"start": v(27.77, -21.3) * mm, "end": v(27.57, -21.15) * mm});
            skArc(sketch, "E13.63.1", {"start": v(27.57, -21.15) * mm, "mid": v(27.75, -20.91) * mm, "end": v(27.93, -20.67) * mm});
            skLineSegment(sketch, "E13.63.2", {"start": v(28.13, -20.82) * mm, "end": v(27.93, -20.67) * mm});
            skArc(sketch, "E13.63.3", {"start": v(27.77, -21.3) * mm, "mid": v(27.95, -21.06) * mm, "end": v(28.13, -20.82) * mm});
            skLineSegment(sketch, "E13.64.0", {"start": v(27, -22.26) * mm, "end": v(26.81, -22.1) * mm});
            skArc(sketch, "E13.64.1", {"start": v(26.81, -22.1) * mm, "mid": v(27, -21.87) * mm, "end": v(27.2, -21.63) * mm});
            skLineSegment(sketch, "E13.64.2", {"start": v(27.4, -21.79) * mm, "end": v(27.2, -21.63) * mm});
            skArc(sketch, "E13.64.3", {"start": v(27, -22.26) * mm, "mid": v(27.2, -22.03) * mm, "end": v(27.4, -21.79) * mm});
            skLineSegment(sketch, "E13.65.0", {"start": v(26.21, -23.2) * mm, "end": v(26.03, -23.03) * mm});
            skArc(sketch, "E13.65.1", {"start": v(26.03, -23.03) * mm, "mid": v(26.23, -22.8) * mm, "end": v(26.42, -22.57) * mm});
            skLineSegment(sketch, "E13.65.2", {"start": v(26.61, -22.73) * mm, "end": v(26.42, -22.57) * mm});
            skArc(sketch, "E13.65.3", {"start": v(26.21, -23.2) * mm, "mid": v(26.41, -22.96) * mm, "end": v(26.61, -22.73) * mm});
            skLineSegment(sketch, "E13.66.0", {"start": v(25.39, -24.1) * mm, "end": v(25.2, -23.92) * mm});
            skArc(sketch, "E13.66.1", {"start": v(25.2, -23.92) * mm, "mid": v(25.41, -23.7) * mm, "end": v(25.62, -23.48) * mm});
            skLineSegment(sketch, "E13.66.2", {"start": v(25.8, -23.65) * mm, "end": v(25.62, -23.48) * mm});
            skArc(sketch, "E13.66.3", {"start": v(25.39, -24.1) * mm, "mid": v(25.6, -23.87) * mm, "end": v(25.8, -23.65) * mm});
            skLineSegment(sketch, "E13.67.0", {"start": v(24.53, -24.96) * mm, "end": v(24.36, -24.79) * mm});
            skArc(sketch, "E13.67.1", {"start": v(24.36, -24.79) * mm, "mid": v(24.57, -24.57) * mm, "end": v(24.79, -24.36) * mm});
            skLineSegment(sketch, "E13.67.2", {"start": v(24.96, -24.53) * mm, "end": v(24.79, -24.36) * mm});
            skArc(sketch, "E13.67.3", {"start": v(24.53, -24.96) * mm, "mid": v(24.75, -24.75) * mm, "end": v(24.96, -24.53) * mm});
            skLineSegment(sketch, "E13.68.0", {"start": v(23.65, -25.8) * mm, "end": v(23.48, -25.62) * mm});
            skArc(sketch, "E13.68.1", {"start": v(23.48, -25.62) * mm, "mid": v(23.7, -25.41) * mm, "end": v(23.92, -25.2) * mm});
            skLineSegment(sketch, "E13.68.2", {"start": v(24.1, -25.39) * mm, "end": v(23.92, -25.2) * mm});
            skArc(sketch, "E13.68.3", {"start": v(23.65, -25.8) * mm, "mid": v(23.87, -25.6) * mm, "end": v(24.1, -25.39) * mm});
            skLineSegment(sketch, "E13.69.0", {"start": v(22.73, -26.61) * mm, "end": v(22.57, -26.42) * mm});
            skArc(sketch, "E13.69.1", {"start": v(22.57, -26.42) * mm, "mid": v(22.8, -26.23) * mm, "end": v(23.03, -26.03) * mm});
            skLineSegment(sketch, "E13.69.2", {"start": v(23.2, -26.21) * mm, "end": v(23.03, -26.03) * mm});
            skArc(sketch, "E13.69.3", {"start": v(22.73, -26.61) * mm, "mid": v(22.96, -26.41) * mm, "end": v(23.2, -26.21) * mm});
            skLineSegment(sketch, "E13.70.0", {"start": v(21.79, -27.4) * mm, "end": v(21.63, -27.2) * mm});
            skArc(sketch, "E13.70.1", {"start": v(21.63, -27.2) * mm, "mid": v(21.87, -27) * mm, "end": v(22.1, -26.81) * mm});
            skLineSegment(sketch, "E13.70.2", {"start": v(22.26, -27) * mm, "end": v(22.1, -26.81) * mm});
            skArc(sketch, "E13.70.3", {"start": v(21.79, -27.4) * mm, "mid": v(22.03, -27.2) * mm, "end": v(22.26, -27) * mm});
            skLineSegment(sketch, "E13.71.0", {"start": v(20.82, -28.13) * mm, "end": v(20.67, -27.93) * mm});
            skArc(sketch, "E13.71.1", {"start": v(20.67, -27.93) * mm, "mid": v(20.91, -27.75) * mm, "end": v(21.15, -27.57) * mm});
            skLineSegment(sketch, "E13.71.2", {"start": v(21.3, -27.77) * mm, "end": v(21.15, -27.57) * mm});
            skArc(sketch, "E13.71.3", {"start": v(20.82, -28.13) * mm, "mid": v(21.06, -27.95) * mm, "end": v(21.3, -27.77) * mm});
            skLineSegment(sketch, "E13.72.0", {"start": v(19.82, -28.84) * mm, "end": v(19.68, -28.64) * mm});
            skArc(sketch, "E13.72.1", {"start": v(19.68, -28.64) * mm, "mid": v(19.93, -28.47) * mm, "end": v(20.18, -28.3) * mm});
            skLineSegment(sketch, "E13.72.2", {"start": v(20.32, -28.5) * mm, "end": v(20.18, -28.3) * mm});
            skArc(sketch, "E13.72.3", {"start": v(19.82, -28.84) * mm, "mid": v(20.08, -28.67) * mm, "end": v(20.32, -28.5) * mm});
            skLineSegment(sketch, "E13.73.0", {"start": v(18.8, -29.52) * mm, "end": v(18.67, -29.3) * mm});
            skArc(sketch, "E13.73.1", {"start": v(18.67, -29.3) * mm, "mid": v(18.93, -29.14) * mm, "end": v(19.18, -28.98) * mm});
            skLineSegment(sketch, "E13.73.2", {"start": v(19.32, -29.19) * mm, "end": v(19.18, -28.98) * mm});
            skArc(sketch, "E13.73.3", {"start": v(18.8, -29.52) * mm, "mid": v(19.06, -29.35) * mm, "end": v(19.32, -29.19) * mm});
            skLineSegment(sketch, "E13.74.0", {"start": v(17.76, -30.16) * mm, "end": v(17.64, -29.94) * mm});
            skArc(sketch, "E13.74.1", {"start": v(17.64, -29.94) * mm, "mid": v(17.9, -29.79) * mm, "end": v(18.16, -29.63) * mm});
            skLineSegment(sketch, "E13.74.2", {"start": v(18.29, -29.84) * mm, "end": v(18.16, -29.63) * mm});
            skArc(sketch, "E13.74.3", {"start": v(17.76, -30.16) * mm, "mid": v(18.03, -30) * mm, "end": v(18.29, -29.84) * mm});
            skLineSegment(sketch, "E13.75.0", {"start": v(16.7, -30.76) * mm, "end": v(16.58, -30.54) * mm});
            skArc(sketch, "E13.75.1", {"start": v(16.58, -30.54) * mm, "mid": v(16.85, -30.4) * mm, "end": v(17.11, -30.24) * mm});
            skLineSegment(sketch, "E13.75.2", {"start": v(17.23, -30.46) * mm, "end": v(17.11, -30.24) * mm});
            skArc(sketch, "E13.75.3", {"start": v(16.7, -30.76) * mm, "mid": v(16.97, -30.61) * mm, "end": v(17.23, -30.46) * mm});
            skLineSegment(sketch, "E13.76.0", {"start": v(15.62, -31.32) * mm, "end": v(15.5, -31.1) * mm});
            skArc(sketch, "E13.76.1", {"start": v(15.5, -31.1) * mm, "mid": v(15.78, -30.96) * mm, "end": v(16.05, -30.82) * mm});
            skLineSegment(sketch, "E13.76.2", {"start": v(16.16, -31.05) * mm, "end": v(16.05, -30.82) * mm});
            skArc(sketch, "E13.76.3", {"start": v(15.62, -31.32) * mm, "mid": v(15.89, -31.19) * mm, "end": v(16.16, -31.05) * mm});
            skLineSegment(sketch, "E13.77.0", {"start": v(14.51, -31.85) * mm, "end": v(14.41, -31.62) * mm});
            skArc(sketch, "E13.77.1", {"start": v(14.41, -31.62) * mm, "mid": v(14.69, -31.5) * mm, "end": v(14.96, -31.36) * mm});
            skLineSegment(sketch, "E13.77.2", {"start": v(15.07, -31.6) * mm, "end": v(14.96, -31.36) * mm});
            skArc(sketch, "E13.77.3", {"start": v(14.51, -31.85) * mm, "mid": v(14.8, -31.72) * mm, "end": v(15.07, -31.6) * mm});
            skLineSegment(sketch, "E13.78.0", {"start": v(13.4, -32.34) * mm, "end": v(13.3, -32.1) * mm});
            skArc(sketch, "E13.78.1", {"start": v(13.3, -32.1) * mm, "mid": v(13.58, -31.99) * mm, "end": v(13.86, -31.87) * mm});
            skLineSegment(sketch, "E13.78.2", {"start": v(13.96, -32.1) * mm, "end": v(13.86, -31.87) * mm});
            skArc(sketch, "E13.78.3", {"start": v(13.4, -32.34) * mm, "mid": v(13.68, -32.22) * mm, "end": v(13.96, -32.1) * mm});
            skLineSegment(sketch, "E13.79.0", {"start": v(12.26, -32.78) * mm, "end": v(12.17, -32.55) * mm});
            skArc(sketch, "E13.79.1", {"start": v(12.17, -32.55) * mm, "mid": v(12.45, -32.44) * mm, "end": v(12.74, -32.33) * mm});
            skLineSegment(sketch, "E13.79.2", {"start": v(12.83, -32.56) * mm, "end": v(12.74, -32.33) * mm});
            skArc(sketch, "E13.79.3", {"start": v(12.26, -32.78) * mm, "mid": v(12.54, -32.68) * mm, "end": v(12.83, -32.56) * mm});
            skLineSegment(sketch, "E13.80.0", {"start": v(11.1, -33.2) * mm, "end": v(11.03, -32.95) * mm});
            skArc(sketch, "E13.80.1", {"start": v(11.03, -32.95) * mm, "mid": v(11.31, -32.86) * mm, "end": v(11.6, -32.76) * mm});
            skLineSegment(sketch, "E13.80.2", {"start": v(11.68, -33) * mm, "end": v(11.6, -32.76) * mm});
            skArc(sketch, "E13.80.3", {"start": v(11.1, -33.2) * mm, "mid": v(11.4, -33.1) * mm, "end": v(11.68, -33) * mm});
            skLineSegment(sketch, "E13.81.0", {"start": v(9.94, -33.56) * mm, "end": v(9.87, -33.32) * mm});
            skArc(sketch, "E13.81.1", {"start": v(9.87, -33.32) * mm, "mid": v(10.16, -33.23) * mm, "end": v(10.45, -33.14) * mm});
            skLineSegment(sketch, "E13.81.2", {"start": v(10.52, -33.38) * mm, "end": v(10.45, -33.14) * mm});
            skArc(sketch, "E13.81.3", {"start": v(9.94, -33.56) * mm, "mid": v(10.23, -33.47) * mm, "end": v(10.52, -33.38) * mm});
            skLineSegment(sketch, "E13.82.0", {"start": v(8.76, -33.89) * mm, "end": v(8.7, -33.64) * mm});
            skArc(sketch, "E13.82.1", {"start": v(8.7, -33.64) * mm, "mid": v(9, -33.57) * mm, "end": v(9.29, -33.49) * mm});
            skLineSegment(sketch, "E13.82.2", {"start": v(9.35, -33.73) * mm, "end": v(9.29, -33.49) * mm});
            skArc(sketch, "E13.82.3", {"start": v(8.76, -33.89) * mm, "mid": v(9.06, -33.8) * mm, "end": v(9.35, -33.73) * mm});
            skLineSegment(sketch, "E13.83.0", {"start": v(7.58, -34.17) * mm, "end": v(7.52, -33.93) * mm});
            skArc(sketch, "E13.83.1", {"start": v(7.52, -33.93) * mm, "mid": v(7.82, -33.86) * mm, "end": v(8.11, -33.79) * mm});
            skLineSegment(sketch, "E13.83.2", {"start": v(8.17, -34.03) * mm, "end": v(8.11, -33.79) * mm});
            skArc(sketch, "E13.83.3", {"start": v(7.58, -34.17) * mm, "mid": v(7.87, -34.1) * mm, "end": v(8.17, -34.03) * mm});
            skLineSegment(sketch, "E13.84.0", {"start": v(6.38, -34.41) * mm, "end": v(6.33, -34.17) * mm});
            skArc(sketch, "E13.84.1", {"start": v(6.33, -34.17) * mm, "mid": v(6.63, -34.11) * mm, "end": v(6.93, -34.05) * mm});
            skLineSegment(sketch, "E13.84.2", {"start": v(6.98, -34.3) * mm, "end": v(6.93, -34.05) * mm});
            skArc(sketch, "E13.84.3", {"start": v(6.38, -34.41) * mm, "mid": v(6.68, -34.36) * mm, "end": v(6.98, -34.3) * mm});
            skLineSegment(sketch, "E13.85.0", {"start": v(5.17, -34.62) * mm, "end": v(5.14, -34.37) * mm});
            skArc(sketch, "E13.85.1", {"start": v(5.14, -34.37) * mm, "mid": v(5.44, -34.32) * mm, "end": v(5.74, -34.27) * mm});
            skLineSegment(sketch, "E13.85.2", {"start": v(5.78, -34.52) * mm, "end": v(5.74, -34.27) * mm});
            skArc(sketch, "E13.85.3", {"start": v(5.17, -34.62) * mm, "mid": v(5.48, -34.57) * mm, "end": v(5.78, -34.52) * mm});
            skLineSegment(sketch, "E13.86.0", {"start": v(3.96, -34.78) * mm, "end": v(3.93, -34.53) * mm});
            skArc(sketch, "E13.86.1", {"start": v(3.93, -34.53) * mm, "mid": v(4.23, -34.5) * mm, "end": v(4.54, -34.45) * mm});
            skLineSegment(sketch, "E13.86.2", {"start": v(4.57, -34.7) * mm, "end": v(4.54, -34.45) * mm});
            skArc(sketch, "E13.86.3", {"start": v(3.96, -34.78) * mm, "mid": v(4.27, -34.74) * mm, "end": v(4.57, -34.7) * mm});
            skLineSegment(sketch, "E13.87.0", {"start": v(2.75, -34.9) * mm, "end": v(2.73, -34.64) * mm});
            skArc(sketch, "E13.87.1", {"start": v(2.73, -34.64) * mm, "mid": v(3.03, -34.62) * mm, "end": v(3.33, -34.6) * mm});
            skLineSegment(sketch, "E13.87.2", {"start": v(3.35, -34.84) * mm, "end": v(3.33, -34.6) * mm});
            skArc(sketch, "E13.87.3", {"start": v(2.75, -34.9) * mm, "mid": v(3.05, -34.87) * mm, "end": v(3.35, -34.84) * mm});
            skLineSegment(sketch, "E13.88.0", {"start": v(1.53, -34.97) * mm, "end": v(1.52, -34.72) * mm});
            skArc(sketch, "E13.88.1", {"start": v(1.52, -34.72) * mm, "mid": v(1.82, -34.7) * mm, "end": v(2.12, -34.69) * mm});
            skLineSegment(sketch, "E13.88.2", {"start": v(2.14, -34.93) * mm, "end": v(2.12, -34.69) * mm});
            skArc(sketch, "E13.88.3", {"start": v(1.53, -34.97) * mm, "mid": v(1.83, -34.95) * mm, "end": v(2.14, -34.93) * mm});
            skLineSegment(sketch, "E13.89.0", {"start": v(0.3, -35) * mm, "end": v(0.3, -34.75) * mm});
            skArc(sketch, "E13.89.1", {"start": v(0.3, -34.75) * mm, "mid": v(0.6, -34.74) * mm, "end": v(0.9, -34.74) * mm});
            skLineSegment(sketch, "E13.89.2", {"start": v(0.92, -34.99) * mm, "end": v(0.9, -34.74) * mm});
            skArc(sketch, "E13.89.3", {"start": v(0.3, -35) * mm, "mid": v(0.61, -35) * mm, "end": v(0.92, -34.99) * mm});
            skLineSegment(sketch, "E13.anchor1", {"start": v(0, 0) * mm, "end": v(0.3, 34.75) * mm, "construction": true});
            skLineSegment(sketch, "E13.anchor2", {"start": v(0, 0) * mm, "end": v(-0.3, -34.75) * mm, "construction": true});
            skLineSegment(sketch, "E14", {"start": v(1.52, 34.72) * mm, "end": v(0, 0) * mm, "construction": true});
            skLineSegment(sketch, "E15.MirrorCS", {"start": v(-35, 0.3) * mm, "end": v(-34.75, 0.3) * mm});
            skLineSegment(sketch, "E16.MirrorCS", {"start": v(-34.97, 1.53) * mm, "end": v(-34.72, 1.52) * mm});
            skLineSegment(sketch, "E17.MirrorCS", {"start": v(-34.9, 2.75) * mm, "end": v(-34.64, 2.73) * mm});
            skArc(sketch, "E18.MirrorCS", {"start": v(-35, 0.3) * mm, "mid": v(-35, 0.61) * mm, "end": v(-34.99, 0.92) * mm});
            skLineSegment(sketch, "E19.MirrorCS", {"start": v(-34.99, 0.92) * mm, "end": v(-34.74, 0.9) * mm});
            skArc(sketch, "E20.MirrorCS", {"start": v(-34.75, 0.3) * mm, "mid": v(-34.74, 0.6) * mm, "end": v(-34.74, 0.9) * mm});
            skArc(sketch, "E21.MirrorCS", {"start": v(-34.97, 1.53) * mm, "mid": v(-34.95, 1.83) * mm, "end": v(-34.93, 2.14) * mm});
            skLineSegment(sketch, "E22.MirrorCS", {"start": v(-34.93, 2.14) * mm, "end": v(-34.69, 2.12) * mm});
            skArc(sketch, "E23.MirrorCS", {"start": v(-34.72, 1.52) * mm, "mid": v(-34.7, 1.82) * mm, "end": v(-34.69, 2.12) * mm});
            skLineSegment(sketch, "E24.MirrorCS", {"start": v(-34.99, -0.92) * mm, "end": v(-34.74, -0.9) * mm});
            skArc(sketch, "E25.MirrorCS", {"start": v(-34.99, -0.92) * mm, "mid": v(-35, -0.61) * mm, "end": v(-35, -0.3) * mm});
            skLineSegment(sketch, "E26.MirrorCS", {"start": v(-35, -0.3) * mm, "end": v(-34.75, -0.3) * mm});
            skArc(sketch, "E27.MirrorCS", {"start": v(-34.74, -0.9) * mm, "mid": v(-34.74, -0.6) * mm, "end": v(-34.75, -0.3) * mm});
            skLineSegment(sketch, "E28.MirrorCS", {"start": v(-34.97, -1.53) * mm, "end": v(-34.72, -1.52) * mm});
            skArc(sketch, "E29.MirrorCS", {"start": v(-34.69, -2.12) * mm, "mid": v(-34.7, -1.82) * mm, "end": v(-34.72, -1.52) * mm});
            skLineSegment(sketch, "E30.MirrorCS", {"start": v(-34.93, -2.14) * mm, "end": v(-34.69, -2.12) * mm});
            skLineSegment(sketch, "E31.MirrorCS", {"start": v(-6.98, 34.3) * mm, "end": v(-6.93, 34.05) * mm});
            skLineSegment(sketch, "E32.MirrorCS", {"start": v(-5.78, 34.52) * mm, "end": v(-5.74, 34.27) * mm});
            skArc(sketch, "E33.MirrorCS", {"start": v(-34.93, -2.14) * mm, "mid": v(-34.95, -1.83) * mm, "end": v(-34.97, -1.53) * mm});
            skLineSegment(sketch, "E34.MirrorCS", {"start": v(-2.75, 34.9) * mm, "end": v(-2.73, 34.64) * mm});
            skArc(sketch, "E35.MirrorCS", {"start": v(-3.93, -34.53) * mm, "mid": v(-4.23, -34.5) * mm, "end": v(-4.54, -34.45) * mm});
            skLineSegment(sketch, "E36.MirrorCS", {"start": v(-3.96, -34.78) * mm, "end": v(-3.93, -34.53) * mm});
            skArc(sketch, "E37.MirrorCS", {"start": v(-6.98, 34.3) * mm, "mid": v(-6.68, 34.36) * mm, "end": v(-6.38, 34.41) * mm});
            skLineSegment(sketch, "E38.MirrorCS", {"start": v(-6.38, 34.41) * mm, "end": v(-6.33, 34.17) * mm});
            skArc(sketch, "E39.MirrorCS", {"start": v(-6.93, 34.05) * mm, "mid": v(-6.63, 34.11) * mm, "end": v(-6.33, 34.17) * mm});
            skLineSegment(sketch, "E40.MirrorCS", {"start": v(-11.68, 33) * mm, "end": v(-11.6, 32.76) * mm});
            skArc(sketch, "E41.MirrorCS", {"start": v(-5.78, 34.52) * mm, "mid": v(-5.48, 34.57) * mm, "end": v(-5.17, 34.62) * mm});
            skArc(sketch, "E42.MirrorCS", {"start": v(-5.74, 34.27) * mm, "mid": v(-5.44, 34.32) * mm, "end": v(-5.14, 34.37) * mm});
            skArc(sketch, "E43.MirrorCS", {"start": v(-2.75, -34.9) * mm, "mid": v(-3.05, -34.87) * mm, "end": v(-3.35, -34.84) * mm});
            skLineSegment(sketch, "E44.MirrorCS", {"start": v(-3.35, -34.84) * mm, "end": v(-3.33, -34.6) * mm});
            skArc(sketch, "E45.MirrorCS", {"start": v(-4.54, 34.45) * mm, "mid": v(-4.23, 34.5) * mm, "end": v(-3.93, 34.53) * mm});
            skArc(sketch, "E46.MirrorCS", {"start": v(-2.73, -34.64) * mm, "mid": v(-3.03, -34.62) * mm, "end": v(-3.33, -34.6) * mm});
            skLineSegment(sketch, "E47.MirrorCS", {"start": v(-2.75, -34.9) * mm, "end": v(-2.73, -34.64) * mm});
            skLineSegment(sketch, "E48.MirrorCS", {"start": v(-34.84, -3.35) * mm, "end": v(-34.6, -3.33) * mm});
            skArc(sketch, "E49.MirrorCS", {"start": v(-3.96, -34.78) * mm, "mid": v(-4.27, -34.74) * mm, "end": v(-4.57, -34.7) * mm});
            skLineSegment(sketch, "E50.MirrorCS", {"start": v(-34.84, 3.35) * mm, "end": v(-34.6, 3.33) * mm});
            skArc(sketch, "E51.MirrorCS", {"start": v(-3.33, 34.6) * mm, "mid": v(-3.03, 34.62) * mm, "end": v(-2.73, 34.64) * mm});
            skLineSegment(sketch, "E52.MirrorCS", {"start": v(-3.35, 34.84) * mm, "end": v(-3.33, 34.6) * mm});
            skLineSegment(sketch, "E53.MirrorCS", {"start": v(-2.14, 34.93) * mm, "end": v(-2.12, 34.69) * mm});
            skLineSegment(sketch, "E54.MirrorCS", {"start": v(-4.57, 34.7) * mm, "end": v(-4.54, 34.45) * mm});
            skArc(sketch, "E55.MirrorCS", {"start": v(-3.35, 34.84) * mm, "mid": v(-3.05, 34.87) * mm, "end": v(-2.75, 34.9) * mm});
            skArc(sketch, "E56.MirrorCS", {"start": v(-34.64, 2.73) * mm, "mid": v(-34.62, 3.03) * mm, "end": v(-34.6, 3.33) * mm});
            skArc(sketch, "E57.MirrorCS", {"start": v(-11.6, 32.76) * mm, "mid": v(-11.31, 32.86) * mm, "end": v(-11.03, 32.95) * mm});
            skLineSegment(sketch, "E58.MirrorCS", {"start": v(-34.52, -5.78) * mm, "end": v(-34.27, -5.74) * mm});
            skLineSegment(sketch, "E59.MirrorCS", {"start": v(-34.78, 3.96) * mm, "end": v(-34.53, 3.93) * mm});
            skLineSegment(sketch, "E60.MirrorCS", {"start": v(-27.4, 21.79) * mm, "end": v(-27.2, 21.63) * mm});
            skLineSegment(sketch, "E61.MirrorCS", {"start": v(-34.78, -3.96) * mm, "end": v(-34.53, -3.93) * mm});
            skLineSegment(sketch, "E62.MirrorCS", {"start": v(-5.17, 34.62) * mm, "end": v(-5.14, 34.37) * mm});
            skLineSegment(sketch, "E63.MirrorCS", {"start": v(-2.14, -34.93) * mm, "end": v(-2.12, -34.69) * mm});
            skLineSegment(sketch, "E64.MirrorCS", {"start": v(-34.7, -4.57) * mm, "end": v(-34.45, -4.54) * mm});
            skLineSegment(sketch, "E65.MirrorCS", {"start": v(-33.73, -9.35) * mm, "end": v(-33.49, -9.29) * mm});
            skLineSegment(sketch, "E66.MirrorCS", {"start": v(-29.52, 18.8) * mm, "end": v(-29.3, 18.67) * mm});
            skLineSegment(sketch, "E67.MirrorCS", {"start": v(-10.52, 33.38) * mm, "end": v(-10.45, 33.14) * mm});
            skArc(sketch, "E68.MirrorCS", {"start": v(-4.57, 34.7) * mm, "mid": v(-4.27, 34.74) * mm, "end": v(-3.96, 34.78) * mm});
            skArc(sketch, "E69.MirrorCS", {"start": v(-34.84, -3.35) * mm, "mid": v(-34.87, -3.05) * mm, "end": v(-34.9, -2.75) * mm});
            skLineSegment(sketch, "E70.MirrorCS", {"start": v(-3.96, 34.78) * mm, "end": v(-3.93, 34.53) * mm});
            skLineSegment(sketch, "E71.MirrorCS", {"start": v(-34.9, -2.75) * mm, "end": v(-34.64, -2.73) * mm});
            skArc(sketch, "E72.MirrorCS", {"start": v(-34.6, -3.33) * mm, "mid": v(-34.62, -3.03) * mm, "end": v(-34.64, -2.73) * mm});
            skArc(sketch, "E73.MirrorCS", {"start": v(-13.86, 31.87) * mm, "mid": v(-13.58, 31.99) * mm, "end": v(-13.3, 32.1) * mm});
            skLineSegment(sketch, "E74.MirrorCS", {"start": v(-32.56, -12.83) * mm, "end": v(-32.33, -12.74) * mm});
            skLineSegment(sketch, "E75.MirrorCS", {"start": v(-34.03, -8.17) * mm, "end": v(-33.79, -8.11) * mm});
            skLineSegment(sketch, "E76.MirrorCS", {"start": v(-13.96, 32.1) * mm, "end": v(-13.86, 31.87) * mm});
            skArc(sketch, "E77.MirrorCS", {"start": v(-34.9, 2.75) * mm, "mid": v(-34.87, 3.05) * mm, "end": v(-34.84, 3.35) * mm});
            skLineSegment(sketch, "E78.MirrorCS", {"start": v(-33.2, -11.1) * mm, "end": v(-32.95, -11.03) * mm});
            skLineSegment(sketch, "E79.MirrorCS", {"start": v(-4.57, -34.7) * mm, "end": v(-4.54, -34.45) * mm});
            skLineSegment(sketch, "E80.MirrorCS", {"start": v(-12.26, 32.78) * mm, "end": v(-12.17, 32.55) * mm});
            skLineSegment(sketch, "E81.MirrorCS", {"start": v(-9.35, -33.73) * mm, "end": v(-9.29, -33.49) * mm});
            skLineSegment(sketch, "E82.MirrorCS", {"start": v(-7.58, 34.17) * mm, "end": v(-7.52, 33.93) * mm});
            skLineSegment(sketch, "E83.MirrorCS", {"start": v(-31.32, -15.62) * mm, "end": v(-31.1, -15.5) * mm});
            skLineSegment(sketch, "E84.MirrorCS", {"start": v(-34.41, -6.38) * mm, "end": v(-34.17, -6.33) * mm});
            skArc(sketch, "E85.MirrorCS", {"start": v(-2.14, 34.93) * mm, "mid": v(-1.83, 34.95) * mm, "end": v(-1.53, 34.97) * mm});
            skLineSegment(sketch, "E86.MirrorCS", {"start": v(-1.53, 34.97) * mm, "end": v(-1.52, 34.72) * mm});
            skArc(sketch, "E87.MirrorCS", {"start": v(-2.12, 34.69) * mm, "mid": v(-1.82, 34.7) * mm, "end": v(-1.52, 34.72) * mm});
            skArc(sketch, "E88.MirrorCS", {"start": v(-8.7, -33.64) * mm, "mid": v(-9, -33.57) * mm, "end": v(-9.29, -33.49) * mm});
            skArc(sketch, "E89.MirrorCS", {"start": v(-34.05, -6.93) * mm, "mid": v(-34.11, -6.63) * mm, "end": v(-34.17, -6.33) * mm});
            skArc(sketch, "E90.MirrorCS", {"start": v(-32.76, -11.6) * mm, "mid": v(-32.86, -11.31) * mm, "end": v(-32.95, -11.03) * mm});
            skArc(sketch, "E91.MirrorCS", {"start": v(-8.11, 33.79) * mm, "mid": v(-7.82, 33.86) * mm, "end": v(-7.52, 33.93) * mm});
            skArc(sketch, "E92.MirrorCS", {"start": v(-12.74, 32.33) * mm, "mid": v(-12.45, 32.44) * mm, "end": v(-12.17, 32.55) * mm});
            skLineSegment(sketch, "E93.MirrorCS", {"start": v(-8.76, -33.89) * mm, "end": v(-8.7, -33.64) * mm});
            skLineSegment(sketch, "E94.MirrorCS", {"start": v(-34.3, -6.98) * mm, "end": v(-34.05, -6.93) * mm});
            skLineSegment(sketch, "E95.MirrorCS", {"start": v(-33, -11.68) * mm, "end": v(-32.76, -11.6) * mm});
            skLineSegment(sketch, "E96.MirrorCS", {"start": v(-8.17, 34.03) * mm, "end": v(-8.11, 33.79) * mm});
            skLineSegment(sketch, "E97.MirrorCS", {"start": v(-12.83, 32.56) * mm, "end": v(-12.74, 32.33) * mm});
            skArc(sketch, "E98.MirrorCS", {"start": v(-9.94, -33.56) * mm, "mid": v(-10.23, -33.47) * mm, "end": v(-10.52, -33.38) * mm});
            skArc(sketch, "E99.MirrorCS", {"start": v(-34.52, -5.78) * mm, "mid": v(-34.57, -5.48) * mm, "end": v(-34.62, -5.17) * mm});
            skArc(sketch, "E100.MirrorCS", {"start": v(-11.68, 33) * mm, "mid": v(-11.4, 33.1) * mm, "end": v(-11.1, 33.2) * mm});
            skLineSegment(sketch, "E101.MirrorCS", {"start": v(-10.52, -33.38) * mm, "end": v(-10.45, -33.14) * mm});
            skLineSegment(sketch, "E102.MirrorCS", {"start": v(-5.78, -34.52) * mm, "end": v(-5.74, -34.27) * mm});
            skLineSegment(sketch, "E103.MirrorCS", {"start": v(-15.07, -31.6) * mm, "end": v(-14.96, -31.36) * mm});
            skLineSegment(sketch, "E104.MirrorCS", {"start": v(-34.62, -5.17) * mm, "end": v(-34.37, -5.14) * mm});
            skLineSegment(sketch, "E105.MirrorCS", {"start": v(-29.52, -18.8) * mm, "end": v(-29.3, -18.67) * mm});
            skLineSegment(sketch, "E106.MirrorCS", {"start": v(-34.7, 4.57) * mm, "end": v(-34.45, 4.54) * mm});
            skLineSegment(sketch, "E107.MirrorCS", {"start": v(-27, 22.26) * mm, "end": v(-26.81, 22.1) * mm});
            skLineSegment(sketch, "E108.MirrorCS", {"start": v(-11.1, 33.2) * mm, "end": v(-11.03, 32.95) * mm});
            skArc(sketch, "E109.MirrorCS", {"start": v(-9.87, -33.32) * mm, "mid": v(-10.16, -33.23) * mm, "end": v(-10.45, -33.14) * mm});
            skArc(sketch, "E110.MirrorCS", {"start": v(-34.27, -5.74) * mm, "mid": v(-34.32, -5.44) * mm, "end": v(-34.37, -5.14) * mm});
            skArc(sketch, "E111.MirrorCS", {"start": v(-27.2, 21.63) * mm, "mid": v(-27, 21.87) * mm, "end": v(-26.81, 22.1) * mm});
            skLineSegment(sketch, "E112.MirrorCS", {"start": v(-9.94, -33.56) * mm, "end": v(-9.87, -33.32) * mm});
            skLineSegment(sketch, "E113.MirrorCS", {"start": v(-5.17, -34.62) * mm, "end": v(-5.14, -34.37) * mm});
            skLineSegment(sketch, "E114.MirrorCS", {"start": v(-22.73, -26.61) * mm, "end": v(-22.57, -26.42) * mm});
            skLineSegment(sketch, "E115.MirrorCS", {"start": v(-18.8, -29.52) * mm, "end": v(-18.67, -29.3) * mm});
            skLineSegment(sketch, "E116.MirrorCS", {"start": v(-33.38, -10.52) * mm, "end": v(-33.14, -10.45) * mm});
            skLineSegment(sketch, "E117.MirrorCS", {"start": v(-31.6, -15.07) * mm, "end": v(-31.36, -14.96) * mm});
            skLineSegment(sketch, "E118.MirrorCS", {"start": v(-29.19, -19.32) * mm, "end": v(-28.98, -19.18) * mm});
            skLineSegment(sketch, "E119.MirrorCS", {"start": v(-32.34, 13.4) * mm, "end": v(-32.1, 13.3) * mm});
            skLineSegment(sketch, "E120.MirrorCS", {"start": v(-33.89, 8.76) * mm, "end": v(-33.64, 8.7) * mm});
            skLineSegment(sketch, "E121.MirrorCS", {"start": v(-20.32, 28.5) * mm, "end": v(-20.18, 28.3) * mm});
            skLineSegment(sketch, "E122.MirrorCS", {"start": v(-30.16, 17.76) * mm, "end": v(-29.94, 17.64) * mm});
            skLineSegment(sketch, "E123.MirrorCS", {"start": v(-16.16, 31.05) * mm, "end": v(-16.05, 30.82) * mm});
            skArc(sketch, "E124.MirrorCS", {"start": v(-1.53, -34.97) * mm, "mid": v(-1.83, -34.95) * mm, "end": v(-2.14, -34.93) * mm});
            skArc(sketch, "E125.MirrorCS", {"start": v(-34.7, -4.57) * mm, "mid": v(-34.74, -4.27) * mm, "end": v(-34.78, -3.96) * mm});
            skArc(sketch, "E126.MirrorCS", {"start": v(-33.73, -9.35) * mm, "mid": v(-33.8, -9.06) * mm, "end": v(-33.89, -8.76) * mm});
            skArc(sketch, "E127.MirrorCS", {"start": v(-10.52, 33.38) * mm, "mid": v(-10.23, 33.47) * mm, "end": v(-9.94, 33.56) * mm});
            skLineSegment(sketch, "E128.MirrorCS", {"start": v(-20.32, -28.5) * mm, "end": v(-20.18, -28.3) * mm});
            skLineSegment(sketch, "E129.MirrorCS", {"start": v(-32.34, -13.4) * mm, "end": v(-32.1, -13.3) * mm});
            skLineSegment(sketch, "E130.MirrorCS", {"start": v(-33.89, -8.76) * mm, "end": v(-33.64, -8.7) * mm});
            skLineSegment(sketch, "E131.MirrorCS", {"start": v(-29.19, 19.32) * mm, "end": v(-28.98, 19.18) * mm});
            skLineSegment(sketch, "E132.MirrorCS", {"start": v(-14.51, 31.85) * mm, "end": v(-14.41, 31.62) * mm});
            skArc(sketch, "E133.MirrorCS", {"start": v(-34.45, -4.54) * mm, "mid": v(-34.5, -4.23) * mm, "end": v(-34.53, -3.93) * mm});
            skArc(sketch, "E134.MirrorCS", {"start": v(-33.49, -9.29) * mm, "mid": v(-33.57, -9) * mm, "end": v(-33.64, -8.7) * mm});
            skArc(sketch, "E135.MirrorCS", {"start": v(-29.3, 18.67) * mm, "mid": v(-29.14, 18.93) * mm, "end": v(-28.98, 19.18) * mm});
            skArc(sketch, "E136.MirrorCS", {"start": v(-10.45, 33.14) * mm, "mid": v(-10.16, 33.23) * mm, "end": v(-9.87, 33.32) * mm});
            skArc(sketch, "E137.MirrorCS", {"start": v(-1.52, -34.72) * mm, "mid": v(-1.82, -34.7) * mm, "end": v(-2.12, -34.69) * mm});
            skArc(sketch, "E138.MirrorCS", {"start": v(-11.03, -32.95) * mm, "mid": v(-11.31, -32.86) * mm, "end": v(-11.6, -32.76) * mm});
            skLineSegment(sketch, "E139.MirrorCS", {"start": v(-34.62, 5.17) * mm, "end": v(-34.37, 5.14) * mm});
            skLineSegment(sketch, "E140.MirrorCS", {"start": v(-31.85, 14.51) * mm, "end": v(-31.62, 14.41) * mm});
            skLineSegment(sketch, "E141.MirrorCS", {"start": v(-33.56, 9.94) * mm, "end": v(-33.32, 9.87) * mm});
            skLineSegment(sketch, "E142.MirrorCS", {"start": v(-15.07, 31.6) * mm, "end": v(-14.96, 31.36) * mm});
            skLineSegment(sketch, "E143.MirrorCS", {"start": v(-19.32, 29.19) * mm, "end": v(-19.18, 28.98) * mm});
            skLineSegment(sketch, "E144.MirrorCS", {"start": v(-19.82, -28.84) * mm, "end": v(-19.68, -28.64) * mm});
            skLineSegment(sketch, "E145.MirrorCS", {"start": v(-11.1, -33.2) * mm, "end": v(-11.03, -32.95) * mm});
            skLineSegment(sketch, "E146.MirrorCS", {"start": v(-6.38, -34.41) * mm, "end": v(-6.33, -34.17) * mm});
            skLineSegment(sketch, "E147.MirrorCS", {"start": v(-32.1, -13.96) * mm, "end": v(-31.87, -13.86) * mm});
            skLineSegment(sketch, "E148.MirrorCS", {"start": v(-29.84, -18.29) * mm, "end": v(-29.63, -18.16) * mm});
            skLineSegment(sketch, "E149.MirrorCS", {"start": v(-27, -22.26) * mm, "end": v(-26.81, -22.1) * mm});
            skArc(sketch, "E150.MirrorCS", {"start": v(-9.35, 33.73) * mm, "mid": v(-9.06, 33.8) * mm, "end": v(-8.76, 33.89) * mm});
            skArc(sketch, "E151.MirrorCS", {"start": v(-13.96, 32.1) * mm, "mid": v(-13.68, 32.22) * mm, "end": v(-13.4, 32.34) * mm});
            skArc(sketch, "E152.MirrorCS", {"start": v(-32.56, -12.83) * mm, "mid": v(-32.68, -12.54) * mm, "end": v(-32.78, -12.26) * mm});
            skArc(sketch, "E153.MirrorCS", {"start": v(-34.03, -8.17) * mm, "mid": v(-34.1, -7.87) * mm, "end": v(-34.17, -7.58) * mm});
            skLineSegment(sketch, "E154.MirrorCS", {"start": v(-8.76, 33.89) * mm, "end": v(-8.7, 33.64) * mm});
            skLineSegment(sketch, "E155.MirrorCS", {"start": v(-13.4, 32.34) * mm, "end": v(-13.3, 32.1) * mm});
            skLineSegment(sketch, "E156.MirrorCS", {"start": v(-32.78, -12.26) * mm, "end": v(-32.55, -12.17) * mm});
            skLineSegment(sketch, "E157.MirrorCS", {"start": v(-34.3, 6.98) * mm, "end": v(-34.05, 6.93) * mm});
            skLineSegment(sketch, "E158.MirrorCS", {"start": v(-34.17, -7.58) * mm, "end": v(-33.93, -7.52) * mm});
            skArc(sketch, "E159.MirrorCS", {"start": v(-32.33, -12.74) * mm, "mid": v(-32.44, -12.45) * mm, "end": v(-32.55, -12.17) * mm});
            skArc(sketch, "E160.MirrorCS", {"start": v(-33.79, -8.11) * mm, "mid": v(-33.86, -7.82) * mm, "end": v(-33.93, -7.52) * mm});
            skArc(sketch, "E161.MirrorCS", {"start": v(-9.29, 33.49) * mm, "mid": v(-9, 33.57) * mm, "end": v(-8.7, 33.64) * mm});
            skLineSegment(sketch, "E162.MirrorCS", {"start": v(-12.26, -32.78) * mm, "end": v(-12.17, -32.55) * mm});
            skLineSegment(sketch, "E163.MirrorCS", {"start": v(-7.58, -34.17) * mm, "end": v(-7.52, -33.93) * mm});
            skLineSegment(sketch, "E164.MirrorCS", {"start": v(-30.46, -17.23) * mm, "end": v(-30.24, -17.11) * mm});
            skLineSegment(sketch, "E165.MirrorCS", {"start": v(-27.77, -21.3) * mm, "end": v(-27.57, -21.15) * mm});
            skLineSegment(sketch, "E166.MirrorCS", {"start": v(-34.41, 6.38) * mm, "end": v(-34.17, 6.33) * mm});
            skLineSegment(sketch, "E167.MirrorCS", {"start": v(-28.84, 19.82) * mm, "end": v(-28.64, 19.68) * mm});
            skLineSegment(sketch, "E168.MirrorCS", {"start": v(-31.32, 15.62) * mm, "end": v(-31.1, 15.5) * mm});
            skLineSegment(sketch, "E169.MirrorCS", {"start": v(-33.2, 11.1) * mm, "end": v(-32.95, 11.03) * mm});
            skLineSegment(sketch, "E170.MirrorCS", {"start": v(-9.35, 33.73) * mm, "end": v(-9.29, 33.49) * mm});
            skLineSegment(sketch, "E171.MirrorCS", {"start": v(-18.29, 29.84) * mm, "end": v(-18.16, 29.63) * mm});
            skArc(sketch, "E172.MirrorCS", {"start": v(-8.76, -33.89) * mm, "mid": v(-9.06, -33.8) * mm, "end": v(-9.35, -33.73) * mm});
            skArc(sketch, "E173.MirrorCS", {"start": v(-33, -11.68) * mm, "mid": v(-33.1, -11.4) * mm, "end": v(-33.2, -11.1) * mm});
            skArc(sketch, "E174.MirrorCS", {"start": v(-31.05, -16.16) * mm, "mid": v(-31.19, -15.89) * mm, "end": v(-31.32, -15.62) * mm});
            skArc(sketch, "E175.MirrorCS", {"start": v(-34.3, -6.98) * mm, "mid": v(-34.36, -6.68) * mm, "end": v(-34.41, -6.38) * mm});
            skArc(sketch, "E176.MirrorCS", {"start": v(-8.17, 34.03) * mm, "mid": v(-7.87, 34.1) * mm, "end": v(-7.58, 34.17) * mm});
            skArc(sketch, "E177.MirrorCS", {"start": v(-12.83, 32.56) * mm, "mid": v(-12.54, 32.68) * mm, "end": v(-12.26, 32.78) * mm});
            skLineSegment(sketch, "E178.MirrorCS", {"start": v(-22.26, -27) * mm, "end": v(-22.1, -26.81) * mm});
            skLineSegment(sketch, "E179.MirrorCS", {"start": v(-13.96, -32.1) * mm, "end": v(-13.86, -31.87) * mm});
            skLineSegment(sketch, "E180.MirrorCS", {"start": v(-32.56, 12.83) * mm, "end": v(-32.33, 12.74) * mm});
            skLineSegment(sketch, "E181.MirrorCS", {"start": v(-30.46, 17.23) * mm, "end": v(-30.24, 17.11) * mm});
            skLineSegment(sketch, "E182.MirrorCS", {"start": v(-28.84, -19.82) * mm, "end": v(-28.64, -19.68) * mm});
            skLineSegment(sketch, "E183.MirrorCS", {"start": v(-27.77, 21.3) * mm, "end": v(-27.57, 21.15) * mm});
            skLineSegment(sketch, "E184.MirrorCS", {"start": v(-34.03, 8.17) * mm, "end": v(-33.79, 8.11) * mm});
            skLineSegment(sketch, "E185.MirrorCS", {"start": v(-16.7, 30.76) * mm, "end": v(-16.58, 30.54) * mm});
            skLineSegment(sketch, "E186.MirrorCS", {"start": v(-0.92, 34.99) * mm, "end": v(-0.9, 34.74) * mm});
            skLineSegment(sketch, "E187.MirrorCS", {"start": v(-0.3, 35) * mm, "end": v(-0.3, 34.75) * mm});
            skArc(sketch, "E188.MirrorCS", {"start": v(-0.9, 34.74) * mm, "mid": v(-0.6, 34.74) * mm, "end": v(-0.3, 34.75) * mm});
            skArc(sketch, "E189.MirrorCS", {"start": v(-0.92, 34.99) * mm, "mid": v(-0.61, 35) * mm, "end": v(-0.3, 35) * mm});
            skArc(sketch, "E190.MirrorCS", {"start": v(-21.63, -27.2) * mm, "mid": v(-21.87, -27) * mm, "end": v(-22.1, -26.81) * mm});
            skArc(sketch, "E191.MirrorCS", {"start": v(-13.3, -32.1) * mm, "mid": v(-13.58, -31.99) * mm, "end": v(-13.86, -31.87) * mm});
            skArc(sketch, "E192.MirrorCS", {"start": v(-30.82, -16.05) * mm, "mid": v(-30.96, -15.78) * mm, "end": v(-31.1, -15.5) * mm});
            skArc(sketch, "E193.MirrorCS", {"start": v(-28.3, -20.18) * mm, "mid": v(-28.47, -19.93) * mm, "end": v(-28.64, -19.68) * mm});
            skArc(sketch, "E194.MirrorCS", {"start": v(-32.55, 12.17) * mm, "mid": v(-32.44, 12.45) * mm, "end": v(-32.33, 12.74) * mm});
            skArc(sketch, "E195.MirrorCS", {"start": v(-33.93, 7.52) * mm, "mid": v(-33.86, 7.82) * mm, "end": v(-33.79, 8.11) * mm});
            skArc(sketch, "E196.MirrorCS", {"start": v(-27.93, 20.67) * mm, "mid": v(-27.75, 20.91) * mm, "end": v(-27.57, 21.15) * mm});
            skArc(sketch, "E197.MirrorCS", {"start": v(-30.54, 16.58) * mm, "mid": v(-30.4, 16.85) * mm, "end": v(-30.24, 17.11) * mm});
            skArc(sketch, "E198.MirrorCS", {"start": v(-17.11, 30.24) * mm, "mid": v(-16.85, 30.4) * mm, "end": v(-16.58, 30.54) * mm});
            skLineSegment(sketch, "E199.MirrorCS", {"start": v(-21.79, -27.4) * mm, "end": v(-21.63, -27.2) * mm});
            skLineSegment(sketch, "E200.MirrorCS", {"start": v(-13.4, -32.34) * mm, "end": v(-13.3, -32.1) * mm});
            skLineSegment(sketch, "E201.MirrorCS", {"start": v(-31.05, -16.16) * mm, "end": v(-30.82, -16.05) * mm});
            skLineSegment(sketch, "E202.MirrorCS", {"start": v(-28.5, -20.32) * mm, "end": v(-28.3, -20.18) * mm});
            skLineSegment(sketch, "E203.MirrorCS", {"start": v(-32.78, 12.26) * mm, "end": v(-32.55, 12.17) * mm});
            skLineSegment(sketch, "E204.MirrorCS", {"start": v(-34.17, 7.58) * mm, "end": v(-33.93, 7.52) * mm});
            skLineSegment(sketch, "E205.MirrorCS", {"start": v(-28.13, 20.82) * mm, "end": v(-27.93, 20.67) * mm});
            skLineSegment(sketch, "E206.MirrorCS", {"start": v(-30.76, 16.7) * mm, "end": v(-30.54, 16.58) * mm});
            skLineSegment(sketch, "E207.MirrorCS", {"start": v(-17.23, 30.46) * mm, "end": v(-17.11, 30.24) * mm});
            skArc(sketch, "E208.MirrorCS", {"start": v(-5.17, -34.62) * mm, "mid": v(-5.48, -34.57) * mm, "end": v(-5.78, -34.52) * mm});
            skArc(sketch, "E209.MirrorCS", {"start": v(-22.73, -26.61) * mm, "mid": v(-22.96, -26.41) * mm, "end": v(-23.2, -26.21) * mm});
            skArc(sketch, "E210.MirrorCS", {"start": v(-18.8, -29.52) * mm, "mid": v(-19.06, -29.35) * mm, "end": v(-19.32, -29.19) * mm});
            skArc(sketch, "E211.MirrorCS", {"start": v(-14.51, -31.85) * mm, "mid": v(-14.8, -31.72) * mm, "end": v(-15.07, -31.6) * mm});
            skArc(sketch, "E212.MirrorCS", {"start": v(-33.38, -10.52) * mm, "mid": v(-33.47, -10.23) * mm, "end": v(-33.56, -9.94) * mm});
            skArc(sketch, "E213.MirrorCS", {"start": v(-31.6, -15.07) * mm, "mid": v(-31.72, -14.8) * mm, "end": v(-31.85, -14.51) * mm});
            skArc(sketch, "E214.MirrorCS", {"start": v(-29.19, -19.32) * mm, "mid": v(-29.35, -19.06) * mm, "end": v(-29.52, -18.8) * mm});
            skArc(sketch, "E215.MirrorCS", {"start": v(-32.34, 13.4) * mm, "mid": v(-32.22, 13.68) * mm, "end": v(-32.1, 13.96) * mm});
            skArc(sketch, "E216.MirrorCS", {"start": v(-33.89, 8.76) * mm, "mid": v(-33.8, 9.06) * mm, "end": v(-33.73, 9.35) * mm});
            skArc(sketch, "E217.MirrorCS", {"start": v(-34.78, 3.96) * mm, "mid": v(-34.74, 4.27) * mm, "end": v(-34.7, 4.57) * mm});
            skArc(sketch, "E218.MirrorCS", {"start": v(-20.32, 28.5) * mm, "mid": v(-20.08, 28.67) * mm, "end": v(-19.82, 28.84) * mm});
            skArc(sketch, "E219.MirrorCS", {"start": v(-27.4, 21.79) * mm, "mid": v(-27.2, 22.03) * mm, "end": v(-27, 22.26) * mm});
            skArc(sketch, "E220.MirrorCS", {"start": v(-30.16, 17.76) * mm, "mid": v(-30, 18.03) * mm, "end": v(-29.84, 18.29) * mm});
            skArc(sketch, "E221.MirrorCS", {"start": v(-16.16, 31.05) * mm, "mid": v(-15.89, 31.19) * mm, "end": v(-15.62, 31.32) * mm});
            skLineSegment(sketch, "E222.MirrorCS", {"start": v(-23.2, -26.21) * mm, "end": v(-23.03, -26.03) * mm});
            skLineSegment(sketch, "E223.MirrorCS", {"start": v(-19.32, -29.19) * mm, "end": v(-19.18, -28.98) * mm});
            skLineSegment(sketch, "E224.MirrorCS", {"start": v(-33.56, -9.94) * mm, "end": v(-33.32, -9.87) * mm});
            skLineSegment(sketch, "E225.MirrorCS", {"start": v(-31.85, -14.51) * mm, "end": v(-31.62, -14.41) * mm});
            skLineSegment(sketch, "E226.MirrorCS", {"start": v(-32.1, 13.96) * mm, "end": v(-31.87, 13.86) * mm});
            skLineSegment(sketch, "E227.MirrorCS", {"start": v(-33.73, 9.35) * mm, "end": v(-33.49, 9.29) * mm});
            skLineSegment(sketch, "E228.MirrorCS", {"start": v(-19.82, 28.84) * mm, "end": v(-19.68, 28.64) * mm});
            skLineSegment(sketch, "E229.MirrorCS", {"start": v(-29.84, 18.29) * mm, "end": v(-29.63, 18.16) * mm});
            skLineSegment(sketch, "E230.MirrorCS", {"start": v(-15.62, 31.32) * mm, "end": v(-15.5, 31.1) * mm});
            skArc(sketch, "E231.MirrorCS", {"start": v(-5.14, -34.37) * mm, "mid": v(-5.44, -34.32) * mm, "end": v(-5.74, -34.27) * mm});
            skArc(sketch, "E232.MirrorCS", {"start": v(-22.57, -26.42) * mm, "mid": v(-22.8, -26.23) * mm, "end": v(-23.03, -26.03) * mm});
            skArc(sketch, "E233.MirrorCS", {"start": v(-18.67, -29.3) * mm, "mid": v(-18.93, -29.14) * mm, "end": v(-19.18, -28.98) * mm});
            skArc(sketch, "E234.MirrorCS", {"start": v(-14.41, -31.62) * mm, "mid": v(-14.69, -31.5) * mm, "end": v(-14.96, -31.36) * mm});
            skArc(sketch, "E235.MirrorCS", {"start": v(-33.14, -10.45) * mm, "mid": v(-33.23, -10.16) * mm, "end": v(-33.32, -9.87) * mm});
            skArc(sketch, "E236.MirrorCS", {"start": v(-31.36, -14.96) * mm, "mid": v(-31.5, -14.69) * mm, "end": v(-31.62, -14.41) * mm});
            skArc(sketch, "E237.MirrorCS", {"start": v(-28.98, -19.18) * mm, "mid": v(-29.14, -18.93) * mm, "end": v(-29.3, -18.67) * mm});
            skArc(sketch, "E238.MirrorCS", {"start": v(-32.1, 13.3) * mm, "mid": v(-31.99, 13.58) * mm, "end": v(-31.87, 13.86) * mm});
            skArc(sketch, "E239.MirrorCS", {"start": v(-33.64, 8.7) * mm, "mid": v(-33.57, 9) * mm, "end": v(-33.49, 9.29) * mm});
            skArc(sketch, "E240.MirrorCS", {"start": v(-34.53, 3.93) * mm, "mid": v(-34.5, 4.23) * mm, "end": v(-34.45, 4.54) * mm});
            skArc(sketch, "E241.MirrorCS", {"start": v(-20.18, 28.3) * mm, "mid": v(-19.93, 28.47) * mm, "end": v(-19.68, 28.64) * mm});
            skArc(sketch, "E242.MirrorCS", {"start": v(-29.94, 17.64) * mm, "mid": v(-29.79, 17.9) * mm, "end": v(-29.63, 18.16) * mm});
            skArc(sketch, "E243.MirrorCS", {"start": v(-16.05, 30.82) * mm, "mid": v(-15.78, 30.96) * mm, "end": v(-15.5, 31.1) * mm});
            skLineSegment(sketch, "E244.MirrorCS", {"start": v(-0.3, -35) * mm, "end": v(-0.3, -34.75) * mm});
            skLineSegment(sketch, "E245.MirrorCS", {"start": v(-14.51, -31.85) * mm, "end": v(-14.41, -31.62) * mm});
            skArc(sketch, "E246.MirrorCS", {"start": v(-19.82, -28.84) * mm, "mid": v(-20.08, -28.67) * mm, "end": v(-20.32, -28.5) * mm});
            skArc(sketch, "E247.MirrorCS", {"start": v(-11.1, -33.2) * mm, "mid": v(-11.4, -33.1) * mm, "end": v(-11.68, -33) * mm});
            skArc(sketch, "E248.MirrorCS", {"start": v(-6.38, -34.41) * mm, "mid": v(-6.68, -34.36) * mm, "end": v(-6.98, -34.3) * mm});
            skArc(sketch, "E249.MirrorCS", {"start": v(-32.1, -13.96) * mm, "mid": v(-32.22, -13.68) * mm, "end": v(-32.34, -13.4) * mm});
            skArc(sketch, "E250.MirrorCS", {"start": v(-29.84, -18.29) * mm, "mid": v(-30, -18.03) * mm, "end": v(-30.16, -17.76) * mm});
            skArc(sketch, "E251.MirrorCS", {"start": v(-34.62, 5.17) * mm, "mid": v(-34.57, 5.48) * mm, "end": v(-34.52, 5.78) * mm});
            skArc(sketch, "E252.MirrorCS", {"start": v(-29.52, 18.8) * mm, "mid": v(-29.35, 19.06) * mm, "end": v(-29.19, 19.32) * mm});
            skArc(sketch, "E253.MirrorCS", {"start": v(-31.85, 14.51) * mm, "mid": v(-31.72, 14.8) * mm, "end": v(-31.6, 15.07) * mm});
            skArc(sketch, "E254.MirrorCS", {"start": v(-33.56, 9.94) * mm, "mid": v(-33.47, 10.23) * mm, "end": v(-33.38, 10.52) * mm});
            skArc(sketch, "E255.MirrorCS", {"start": v(-15.07, 31.6) * mm, "mid": v(-14.8, 31.72) * mm, "end": v(-14.51, 31.85) * mm});
            skArc(sketch, "E256.MirrorCS", {"start": v(-19.32, 29.19) * mm, "mid": v(-19.06, 29.35) * mm, "end": v(-18.8, 29.52) * mm});
            skLineSegment(sketch, "E257.MirrorCS", {"start": v(-16.16, -31.05) * mm, "end": v(-16.05, -30.82) * mm});
            skLineSegment(sketch, "E258.MirrorCS", {"start": v(-11.68, -33) * mm, "end": v(-11.6, -32.76) * mm});
            skLineSegment(sketch, "E259.MirrorCS", {"start": v(-6.98, -34.3) * mm, "end": v(-6.93, -34.05) * mm});
            skLineSegment(sketch, "E260.MirrorCS", {"start": v(-30.16, -17.76) * mm, "end": v(-29.94, -17.64) * mm});
            skLineSegment(sketch, "E261.MirrorCS", {"start": v(-27.4, -21.79) * mm, "end": v(-27.2, -21.63) * mm});
            skLineSegment(sketch, "E262.MirrorCS", {"start": v(-34.52, 5.78) * mm, "end": v(-34.27, 5.74) * mm});
            skLineSegment(sketch, "E263.MirrorCS", {"start": v(-31.6, 15.07) * mm, "end": v(-31.36, 14.96) * mm});
            skLineSegment(sketch, "E264.MirrorCS", {"start": v(-33.38, 10.52) * mm, "end": v(-33.14, 10.45) * mm});
            skLineSegment(sketch, "E265.MirrorCS", {"start": v(-9.94, 33.56) * mm, "end": v(-9.87, 33.32) * mm});
            skLineSegment(sketch, "E266.MirrorCS", {"start": v(-18.8, 29.52) * mm, "end": v(-18.67, 29.3) * mm});
            skArc(sketch, "E267.MirrorCS", {"start": v(-31.87, -13.86) * mm, "mid": v(-31.99, -13.58) * mm, "end": v(-32.1, -13.3) * mm});
            skArc(sketch, "E268.MirrorCS", {"start": v(-29.63, -18.16) * mm, "mid": v(-29.79, -17.9) * mm, "end": v(-29.94, -17.64) * mm});
            skArc(sketch, "E269.MirrorCS", {"start": v(-26.81, -22.1) * mm, "mid": v(-27, -21.87) * mm, "end": v(-27.2, -21.63) * mm});
            skArc(sketch, "E270.MirrorCS", {"start": v(-34.37, 5.14) * mm, "mid": v(-34.32, 5.44) * mm, "end": v(-34.27, 5.74) * mm});
            skArc(sketch, "E271.MirrorCS", {"start": v(-31.62, 14.41) * mm, "mid": v(-31.5, 14.69) * mm, "end": v(-31.36, 14.96) * mm});
            skArc(sketch, "E272.MirrorCS", {"start": v(-33.32, 9.87) * mm, "mid": v(-33.23, 10.16) * mm, "end": v(-33.14, 10.45) * mm});
            skArc(sketch, "E273.MirrorCS", {"start": v(-14.96, 31.36) * mm, "mid": v(-14.69, 31.5) * mm, "end": v(-14.41, 31.62) * mm});
            skArc(sketch, "E274.MirrorCS", {"start": v(-19.18, 28.98) * mm, "mid": v(-18.93, 29.14) * mm, "end": v(-18.67, 29.3) * mm});
            skArc(sketch, "E275.MirrorCS", {"start": v(-19.68, -28.64) * mm, "mid": v(-19.93, -28.47) * mm, "end": v(-20.18, -28.3) * mm});
            skArc(sketch, "E276.MirrorCS", {"start": v(-15.5, -31.1) * mm, "mid": v(-15.78, -30.96) * mm, "end": v(-16.05, -30.82) * mm});
            skArc(sketch, "E277.MirrorCS", {"start": v(-6.33, -34.17) * mm, "mid": v(-6.63, -34.11) * mm, "end": v(-6.93, -34.05) * mm});
            skLineSegment(sketch, "E278.MirrorCS", {"start": v(-1.53, -34.97) * mm, "end": v(-1.52, -34.72) * mm});
            skLineSegment(sketch, "E279.MirrorCS", {"start": v(-15.62, -31.32) * mm, "end": v(-15.5, -31.1) * mm});
            skArc(sketch, "E280.MirrorCS", {"start": v(-28.84, 19.82) * mm, "mid": v(-28.67, 20.08) * mm, "end": v(-28.5, 20.32) * mm});
            skArc(sketch, "E281.MirrorCS", {"start": v(-31.32, 15.62) * mm, "mid": v(-31.19, 15.89) * mm, "end": v(-31.05, 16.16) * mm});
            skArc(sketch, "E282.MirrorCS", {"start": v(-33.2, 11.1) * mm, "mid": v(-33.1, 11.4) * mm, "end": v(-33, 11.68) * mm});
            skArc(sketch, "E283.MirrorCS", {"start": v(-18.29, 29.84) * mm, "mid": v(-18.03, 30) * mm, "end": v(-17.76, 30.16) * mm});
            skArc(sketch, "E284.MirrorCS", {"start": v(-12.26, -32.78) * mm, "mid": v(-12.54, -32.68) * mm, "end": v(-12.83, -32.56) * mm});
            skArc(sketch, "E285.MirrorCS", {"start": v(-30.46, -17.23) * mm, "mid": v(-30.61, -16.97) * mm, "end": v(-30.76, -16.7) * mm});
            skArc(sketch, "E286.MirrorCS", {"start": v(-27.77, -21.3) * mm, "mid": v(-27.95, -21.06) * mm, "end": v(-28.13, -20.82) * mm});
            skArc(sketch, "E287.MirrorCS", {"start": v(-34.41, 6.38) * mm, "mid": v(-34.36, 6.68) * mm, "end": v(-34.3, 6.98) * mm});
            skLineSegment(sketch, "E288.MirrorCS", {"start": v(-17.76, 30.16) * mm, "end": v(-17.64, 29.94) * mm});
            skLineSegment(sketch, "E289.MirrorCS", {"start": v(-21.3, -27.77) * mm, "end": v(-21.15, -27.57) * mm});
            skLineSegment(sketch, "E290.MirrorCS", {"start": v(-12.83, -32.56) * mm, "end": v(-12.74, -32.33) * mm});
            skLineSegment(sketch, "E291.MirrorCS", {"start": v(-8.17, -34.03) * mm, "end": v(-8.11, -33.79) * mm});
            skLineSegment(sketch, "E292.MirrorCS", {"start": v(-30.76, -16.7) * mm, "end": v(-30.54, -16.58) * mm});
            skLineSegment(sketch, "E293.MirrorCS", {"start": v(-28.13, -20.82) * mm, "end": v(-27.93, -20.67) * mm});
            skLineSegment(sketch, "E294.MirrorCS", {"start": v(-28.5, 20.32) * mm, "end": v(-28.3, 20.18) * mm});
            skLineSegment(sketch, "E295.MirrorCS", {"start": v(-31.05, 16.16) * mm, "end": v(-30.82, 16.05) * mm});
            skLineSegment(sketch, "E296.MirrorCS", {"start": v(-33, 11.68) * mm, "end": v(-32.76, 11.6) * mm});
            skArc(sketch, "E297.MirrorCS", {"start": v(-12.17, -32.55) * mm, "mid": v(-12.45, -32.44) * mm, "end": v(-12.74, -32.33) * mm});
            skArc(sketch, "E298.MirrorCS", {"start": v(-7.52, -33.93) * mm, "mid": v(-7.82, -33.86) * mm, "end": v(-8.11, -33.79) * mm});
            skArc(sketch, "E299.MirrorCS", {"start": v(-30.24, -17.11) * mm, "mid": v(-30.4, -16.85) * mm, "end": v(-30.54, -16.58) * mm});
            skArc(sketch, "E300.MirrorCS", {"start": v(-27.57, -21.15) * mm, "mid": v(-27.75, -20.91) * mm, "end": v(-27.93, -20.67) * mm});
            skArc(sketch, "E301.MirrorCS", {"start": v(-34.17, 6.33) * mm, "mid": v(-34.11, 6.63) * mm, "end": v(-34.05, 6.93) * mm});
            skArc(sketch, "E302.MirrorCS", {"start": v(-28.64, 19.68) * mm, "mid": v(-28.47, 19.93) * mm, "end": v(-28.3, 20.18) * mm});
            skArc(sketch, "E303.MirrorCS", {"start": v(-31.1, 15.5) * mm, "mid": v(-30.96, 15.78) * mm, "end": v(-30.82, 16.05) * mm});
            skArc(sketch, "E304.MirrorCS", {"start": v(-32.95, 11.03) * mm, "mid": v(-32.86, 11.31) * mm, "end": v(-32.76, 11.6) * mm});
            skArc(sketch, "E305.MirrorCS", {"start": v(-18.16, 29.63) * mm, "mid": v(-17.9, 29.79) * mm, "end": v(-17.64, 29.94) * mm});
            skLineSegment(sketch, "E306.MirrorCS", {"start": v(-20.82, -28.13) * mm, "end": v(-20.67, -27.93) * mm});
            skLineSegment(sketch, "E307.MirrorCS", {"start": v(-16.7, -30.76) * mm, "end": v(-16.58, -30.54) * mm});
            skArc(sketch, "E308.MirrorCS", {"start": v(-21.79, -27.4) * mm, "mid": v(-22.03, -27.2) * mm, "end": v(-22.26, -27) * mm});
            skArc(sketch, "E309.MirrorCS", {"start": v(-17.76, -30.16) * mm, "mid": v(-18.03, -30) * mm, "end": v(-18.29, -29.84) * mm});
            skArc(sketch, "E310.MirrorCS", {"start": v(-13.4, -32.34) * mm, "mid": v(-13.68, -32.22) * mm, "end": v(-13.96, -32.1) * mm});
            skArc(sketch, "E311.MirrorCS", {"start": v(-28.5, -20.32) * mm, "mid": v(-28.67, -20.08) * mm, "end": v(-28.84, -19.82) * mm});
            skArc(sketch, "E312.MirrorCS", {"start": v(-34.17, 7.58) * mm, "mid": v(-34.1, 7.87) * mm, "end": v(-34.03, 8.17) * mm});
            skArc(sketch, "E313.MirrorCS", {"start": v(-28.13, 20.82) * mm, "mid": v(-27.95, 21.06) * mm, "end": v(-27.77, 21.3) * mm});
            skArc(sketch, "E314.MirrorCS", {"start": v(-30.76, 16.7) * mm, "mid": v(-30.61, 16.97) * mm, "end": v(-30.46, 17.23) * mm});
            skArc(sketch, "E315.MirrorCS", {"start": v(-32.78, 12.26) * mm, "mid": v(-32.68, 12.54) * mm, "end": v(-32.56, 12.83) * mm});
            skArc(sketch, "E316.MirrorCS", {"start": v(-17.23, 30.46) * mm, "mid": v(-16.97, 30.61) * mm, "end": v(-16.7, 30.76) * mm});
            skLineSegment(sketch, "E317.MirrorCS", {"start": v(-18.29, -29.84) * mm, "end": v(-18.16, -29.63) * mm});
            skArc(sketch, "E318.MirrorCS", {"start": v(-17.64, -29.94) * mm, "mid": v(-17.9, -29.79) * mm, "end": v(-18.16, -29.63) * mm});
            skLineSegment(sketch, "E319.MirrorCS", {"start": v(-17.76, -30.16) * mm, "end": v(-17.64, -29.94) * mm});
            skArc(sketch, "E320.MirrorCS", {"start": v(-0.3, -35) * mm, "mid": v(-0.61, -35) * mm, "end": v(-0.92, -34.99) * mm});
            skLineSegment(sketch, "E321.MirrorCS", {"start": v(-0.92, -34.99) * mm, "end": v(-0.9, -34.74) * mm});
            skLineSegment(sketch, "E322.MirrorCS", {"start": v(-26.61, -22.73) * mm, "end": v(-26.42, -22.57) * mm});
            skArc(sketch, "E323.MirrorCS", {"start": v(-0.3, -34.75) * mm, "mid": v(-0.6, -34.74) * mm, "end": v(-0.9, -34.74) * mm});
            skLineSegment(sketch, "E324.MirrorCS", {"start": v(-26.21, -23.2) * mm, "end": v(-26.03, -23.03) * mm});
            skLineSegment(sketch, "E325.MirrorCS", {"start": v(-24.1, 25.39) * mm, "end": v(-23.92, 25.2) * mm});
            skArc(sketch, "E326.MirrorCS", {"start": v(-15.62, -31.32) * mm, "mid": v(-15.89, -31.19) * mm, "end": v(-16.16, -31.05) * mm});
            skArc(sketch, "E327.MirrorCS", {"start": v(-27, -22.26) * mm, "mid": v(-27.2, -22.03) * mm, "end": v(-27.4, -21.79) * mm});
            skLineSegment(sketch, "E328.MirrorCS", {"start": v(-26.21, 23.2) * mm, "end": v(-26.03, 23.03) * mm});
            skLineSegment(sketch, "E329.MirrorCS", {"start": v(-22.73, 26.61) * mm, "end": v(-22.57, 26.42) * mm});
            skLineSegment(sketch, "E330.MirrorCS", {"start": v(-26.61, 22.73) * mm, "end": v(-26.42, 22.57) * mm});
            skLineSegment(sketch, "E331.MirrorCS", {"start": v(-23.2, 26.21) * mm, "end": v(-23.03, 26.03) * mm});
            skLineSegment(sketch, "E332.MirrorCS", {"start": v(-23.65, -25.8) * mm, "end": v(-23.48, -25.62) * mm});
            skArc(sketch, "E333.MirrorCS", {"start": v(-20.82, -28.13) * mm, "mid": v(-21.06, -27.95) * mm, "end": v(-21.3, -27.77) * mm});
            skArc(sketch, "E334.MirrorCS", {"start": v(-16.7, -30.76) * mm, "mid": v(-16.97, -30.61) * mm, "end": v(-17.23, -30.46) * mm});
            skArc(sketch, "E335.MirrorCS", {"start": v(-7.58, -34.17) * mm, "mid": v(-7.87, -34.1) * mm, "end": v(-8.17, -34.03) * mm});
            skLineSegment(sketch, "E336.MirrorCS", {"start": v(-17.23, -30.46) * mm, "end": v(-17.11, -30.24) * mm});
            skArc(sketch, "E337.MirrorCS", {"start": v(-20.67, -27.93) * mm, "mid": v(-20.91, -27.75) * mm, "end": v(-21.15, -27.57) * mm});
            skArc(sketch, "E338.MirrorCS", {"start": v(-16.58, -30.54) * mm, "mid": v(-16.85, -30.4) * mm, "end": v(-17.11, -30.24) * mm});
            skLineSegment(sketch, "E339.MirrorCS", {"start": v(-24.53, -24.96) * mm, "end": v(-24.36, -24.79) * mm});
            skLineSegment(sketch, "E340.MirrorCS", {"start": v(-25.8, 23.65) * mm, "end": v(-25.62, 23.48) * mm});
            skLineSegment(sketch, "E341.MirrorCS", {"start": v(-22.26, 27) * mm, "end": v(-22.1, 26.81) * mm});
            skLineSegment(sketch, "E342.MirrorCS", {"start": v(-24.53, 24.96) * mm, "end": v(-24.36, 24.79) * mm});
            skLineSegment(sketch, "E343.MirrorCS", {"start": v(-25.8, -23.65) * mm, "end": v(-25.62, -23.48) * mm});
            skLineSegment(sketch, "E344.MirrorCS", {"start": v(-20.82, 28.13) * mm, "end": v(-20.67, 27.93) * mm});
            skArc(sketch, "E345.MirrorCS", {"start": v(-25.2, -23.92) * mm, "mid": v(-25.41, -23.7) * mm, "end": v(-25.62, -23.48) * mm});
            skArc(sketch, "E346.MirrorCS", {"start": v(-21.15, 27.57) * mm, "mid": v(-20.91, 27.75) * mm, "end": v(-20.67, 27.93) * mm});
            skArc(sketch, "E347.MirrorCS", {"start": v(-24.79, 24.36) * mm, "mid": v(-24.57, 24.57) * mm, "end": v(-24.36, 24.79) * mm});
            skLineSegment(sketch, "E348.MirrorCS", {"start": v(-25.39, -24.1) * mm, "end": v(-25.2, -23.92) * mm});
            skLineSegment(sketch, "E349.MirrorCS", {"start": v(-21.3, 27.77) * mm, "end": v(-21.15, 27.57) * mm});
            skLineSegment(sketch, "E350.MirrorCS", {"start": v(-24.96, 24.53) * mm, "end": v(-24.79, 24.36) * mm});
            skArc(sketch, "E351.MirrorCS", {"start": v(-26.21, -23.2) * mm, "mid": v(-26.41, -22.96) * mm, "end": v(-26.61, -22.73) * mm});
            skArc(sketch, "E352.MirrorCS", {"start": v(-24.1, 25.39) * mm, "mid": v(-23.87, 25.6) * mm, "end": v(-23.65, 25.8) * mm});
            skLineSegment(sketch, "E353.MirrorCS", {"start": v(-23.65, 25.8) * mm, "end": v(-23.48, 25.62) * mm});
            skArc(sketch, "E354.MirrorCS", {"start": v(-26.03, -23.03) * mm, "mid": v(-26.23, -22.8) * mm, "end": v(-26.42, -22.57) * mm});
            skArc(sketch, "E355.MirrorCS", {"start": v(-23.92, 25.2) * mm, "mid": v(-23.7, 25.41) * mm, "end": v(-23.48, 25.62) * mm});
            skArc(sketch, "E356.MirrorCS", {"start": v(-23.65, -25.8) * mm, "mid": v(-23.87, -25.6) * mm, "end": v(-24.1, -25.39) * mm});
            skArc(sketch, "E357.MirrorCS", {"start": v(-26.61, 22.73) * mm, "mid": v(-26.41, 22.96) * mm, "end": v(-26.21, 23.2) * mm});
            skArc(sketch, "E358.MirrorCS", {"start": v(-23.2, 26.21) * mm, "mid": v(-22.96, 26.41) * mm, "end": v(-22.73, 26.61) * mm});
            skLineSegment(sketch, "E359.MirrorCS", {"start": v(-24.1, -25.39) * mm, "end": v(-23.92, -25.2) * mm});
            skArc(sketch, "E360.MirrorCS", {"start": v(-23.48, -25.62) * mm, "mid": v(-23.7, -25.41) * mm, "end": v(-23.92, -25.2) * mm});
            skArc(sketch, "E361.MirrorCS", {"start": v(-26.42, 22.57) * mm, "mid": v(-26.23, 22.8) * mm, "end": v(-26.03, 23.03) * mm});
            skArc(sketch, "E362.MirrorCS", {"start": v(-23.03, 26.03) * mm, "mid": v(-22.8, 26.23) * mm, "end": v(-22.57, 26.42) * mm});
            skArc(sketch, "E363.MirrorCS", {"start": v(-25.8, 23.65) * mm, "mid": v(-25.6, 23.87) * mm, "end": v(-25.39, 24.1) * mm});
            skArc(sketch, "E364.MirrorCS", {"start": v(-22.26, 27) * mm, "mid": v(-22.03, 27.2) * mm, "end": v(-21.79, 27.4) * mm});
            skArc(sketch, "E365.MirrorCS", {"start": v(-24.53, -24.96) * mm, "mid": v(-24.75, -24.75) * mm, "end": v(-24.96, -24.53) * mm});
            skLineSegment(sketch, "E366.MirrorCS", {"start": v(-21.79, 27.4) * mm, "end": v(-21.63, 27.2) * mm});
            skLineSegment(sketch, "E367.MirrorCS", {"start": v(-24.96, -24.53) * mm, "end": v(-24.79, -24.36) * mm});
            skLineSegment(sketch, "E368.MirrorCS", {"start": v(-25.39, 24.1) * mm, "end": v(-25.2, 23.92) * mm});
            skArc(sketch, "E369.MirrorCS", {"start": v(-24.36, -24.79) * mm, "mid": v(-24.57, -24.57) * mm, "end": v(-24.79, -24.36) * mm});
            skArc(sketch, "E370.MirrorCS", {"start": v(-25.62, 23.48) * mm, "mid": v(-25.41, 23.7) * mm, "end": v(-25.2, 23.92) * mm});
            skArc(sketch, "E371.MirrorCS", {"start": v(-22.1, 26.81) * mm, "mid": v(-21.87, 27) * mm, "end": v(-21.63, 27.2) * mm});
            skArc(sketch, "E372.MirrorCS", {"start": v(-25.39, -24.1) * mm, "mid": v(-25.6, -23.87) * mm, "end": v(-25.8, -23.65) * mm});
            skArc(sketch, "E373.MirrorCS", {"start": v(-24.96, 24.53) * mm, "mid": v(-24.75, 24.75) * mm, "end": v(-24.53, 24.96) * mm});
            skArc(sketch, "E374.MirrorCS", {"start": v(-21.3, 27.77) * mm, "mid": v(-21.06, 27.95) * mm, "end": v(-20.82, 28.13) * mm});
            skLineSegment(sketch, "E375.MirrorCS", {"start": v(0, 0) * mm, "end": v(-0.3, 34.75) * mm, "construction": true});
            skLineSegment(sketch, "E376.MirrorCS", {"start": v(0, 0) * mm, "end": v(-0.92, 34.99) * mm, "construction": true});
            skLineSegment(sketch, "E377.MirrorCS", {"start": v(-0.3, 35) * mm, "end": v(0, 0) * mm, "construction": true});
            skLineSegment(sketch, "E378.MirrorCS", {"start": v(0, 0) * mm, "end": v(0.3, -34.75) * mm, "construction": true});
            skLineSegment(sketch, "E379.MirrorCS", {"start": v(-1.52, 34.72) * mm, "end": v(0, 0) * mm, "construction": true});
            skSolve(sketch);
        }
        {
            var Q0;
            Q0=qSketchRegion(id+"F3",true);
            extrude(context, id + "F4", {"entities" : qUnion([Q0]), "operationType" : NewBodyOperationType.REMOVE, "endBound" : BoundingType.UP_TO_NEXT, "oppositeDirection" : true, "depth" : 25 * mm});
        }
    });
